FCSTD DOCUMENT  (FreeCAD 1.0R39109 (Git))
Label: Car_roof_Mount
License: All rights reserved
LicenseURL: https://en.wikipedia.org/wiki/All_rights_reserved
objects: Part::Feature×219, Part::Cylinder×108, App::Part×48, Part::MultiFuse×18, Part::Box×15, Part::Cut×6, Part::Torus×5, Part::FeaturePython×4, Part::Fillet×3, TechDraw::DrawSVGTemplate×1, TechDraw::DrawViewPart×1, TechDraw::DrawViewDimension×1, TechDraw::DrawPage×1, Sketcher::SketchObject×1, Part::Extrusion×1
note: 382 computed .brp shape members not serialized (recipe doc carries the construction recipe); baked Part::Feature solids carry a one-line shape summary decoded from their .brp

FEATURE [Part::Box] Box  label="Cube"
  AttacherType = Attacher::AttachEngine3D
  Height = 3.25
  Length = 762
  Placement = pos=(1065,96,7) rot=(0,0,1;1.5708rad)
  Width = 914.4
FEATURE [Part::Cylinder] Cylinder  label="base00"
  Angle = 360
  AttacherType = Attacher::AttachEngine3D
  FirstAngle = 0
  Height = 965.2
  Placement = pos=(12.7,0,0) rot=(-0.57735,0.57735,0.57735;2.0944rad)
  Radius = 12.7
  SecondAngle = 0
FEATURE [Part::Cylinder] Cylinder002  label="base02"
  Angle = 360
  AttacherType = Attacher::AttachEngine3D
  FirstAngle = 0
  Height = 1244.6
  Placement = pos=(0,12.7,0) rot=(0,1,0;1.5708rad)
  Radius = 12.7
  SecondAngle = 0
FEATURE [Part::Cylinder] Cylinder003  label="base03"
  Angle = 360
  AttacherType = Attacher::AttachEngine3D
  FirstAngle = 0
  Height = 1244.6
  Placement = pos=(0,952.5,0) rot=(0,1,0;1.5708rad)
  Radius = 12.7
  SecondAngle = 0
FEATURE [Part::Cylinder] Cylinder004  label="mount01"
  Angle = 360
  AttacherType = Attacher::AttachEngine3D
  FirstAngle = 0
  Height = 76.2
  Placement = pos=(1235.62,12.7,-3.72) rot=(0.382683,0,0.92388;3.14159rad)
  Radius = 12.7
  SecondAngle = 0
FEATURE [Part::Cylinder] Cylinder005  label="mount002"
  Angle = 360
  AttacherType = Attacher::AttachEngine3D
  FirstAngle = 0
  Height = 76.2
  Placement = pos=(1235.62,952.5,-3.72) rot=(0.382683,0,0.92388;3.14159rad)
  Radius = 12.7
  SecondAngle = 0
FEATURE [Part::Torus] Torus
  Angle1 = -180
  Angle2 = 180
  Angle3 = 14.3
  AttacherType = Attacher::AttachEngine3D
  Placement = pos=(-2495,471.5,50.8) rot=(0,0,-1;0.122173rad)
  Radius1 = 3810
  Radius2 = 12.7
FEATURE [Part::Cylinder] Cylinder006  label="base004"
  Angle = 360
  AttacherType = Attacher::AttachEngine3D
  FirstAngle = 0
  Height = 965.2
  Placement = pos=(-63.5,0,76.2) rot=(-0.57735,0.57735,0.57735;2.0944rad)
  Radius = 12.7
  SecondAngle = 0
FEATURE [Part::Torus] Torus001
  Angle1 = -180
  Angle2 = 180
  Angle3 = 16.28
  AttacherType = Attacher::AttachEngine3D
  Placement = pos=(519.042,-57.4562,-4703.18) rot=(0.533716,0.602162,0.593758;4.10898rad)
  Radius1 = 4817.1
  Radius2 = 12.7
FEATURE [Part::Torus] Torus002
  Angle1 = -180
  Angle2 = 180
  Angle3 = 16.28
  AttacherType = Attacher::AttachEngine3D
  Placement = pos=(519.042,889,-4703.18) rot=(0.533716,0.602162,0.593758;4.10898rad)
  Radius1 = 4817.1
  Radius2 = 12.7
FEATURE [Part::Cylinder] Cylinder007  label="base005"
  Angle = 360
  AttacherType = Attacher::AttachEngine3D
  FirstAngle = 0
  Height = 965.2
  Placement = pos=(1089.2,0,0) rot=(0.57735,-0.57735,-0.57735;4.18879rad)
  Radius = 6.35
  SecondAngle = 0
FEATURE [Part::Cylinder] Cylinder008  label="base006"
  Angle = 360
  AttacherType = Attacher::AttachEngine3D
  FirstAngle = 0
  Height = 965.2
  Placement = pos=(919.2,0,0) rot=(0.57735,-0.57735,-0.57735;4.18879rad)
  Radius = 6.35
  SecondAngle = 0
FEATURE [Part::Cylinder] Cylinder009  label="base007"
  Angle = 360
  AttacherType = Attacher::AttachEngine3D
  FirstAngle = 0
  Height = 965.2
  Placement = pos=(749.2,0,0) rot=(0.57735,-0.57735,-0.57735;4.18879rad)
  Radius = 6.35
  SecondAngle = 0
FEATURE [Part::Cylinder] Cylinder010  label="base008"
  Angle = 360
  AttacherType = Attacher::AttachEngine3D
  FirstAngle = 0
  Height = 965.2
  Placement = pos=(579.2,0,0) rot=(0.57735,-0.57735,-0.57735;4.18879rad)
  Radius = 6.35
  SecondAngle = 0
FEATURE [Part::Cylinder] Cylinder011  label="base009"
  Angle = 360
  AttacherType = Attacher::AttachEngine3D
  FirstAngle = 0
  Height = 965.2
  Placement = pos=(409.2,0,0) rot=(0.57735,-0.57735,-0.57735;4.18879rad)
  Radius = 6.35
  SecondAngle = 0
FEATURE [Part::Cylinder] Cylinder012  label="base010"
  Angle = 360
  AttacherType = Attacher::AttachEngine3D
  FirstAngle = 0
  Height = 790
  Placement = pos=(0,149.7,0) rot=(0,1,0;1.5708rad)
  Radius = 6.35
  SecondAngle = 0
FEATURE [Part::Cylinder] Cylinder013  label="base011"
  Angle = 360
  AttacherType = Attacher::AttachEngine3D
  FirstAngle = 0
  Height = 790
  Placement = pos=(0,279.7,0) rot=(0,1,0;1.5708rad)
  Radius = 6.35
  SecondAngle = 0
FEATURE [Part::Cylinder] Cylinder014  label="base012"
  Angle = 360
  AttacherType = Attacher::AttachEngine3D
  FirstAngle = 0
  Height = 790
  Placement = pos=(0,409.7,0) rot=(0,1,0;1.5708rad)
  Radius = 6.35
  SecondAngle = 0
FEATURE [Part::Cylinder] Cylinder015  label="base013"
  Angle = 360
  AttacherType = Attacher::AttachEngine3D
  FirstAngle = 0
  Height = 790
  Placement = pos=(0,539.7,0) rot=(0,1,0;1.5708rad)
  Radius = 6.35
  SecondAngle = 0
FEATURE [Part::Cylinder] Cylinder016  label="base014"
  Angle = 360
  AttacherType = Attacher::AttachEngine3D
  FirstAngle = 0
  Height = 790
  Placement = pos=(0,669.7,0) rot=(0,1,0;1.5708rad)
  Radius = 6.35
  SecondAngle = 0
FEATURE [Part::Cylinder] Cylinder017  label="base015"
  Angle = 360
  AttacherType = Attacher::AttachEngine3D
  FirstAngle = 0
  Height = 790
  Placement = pos=(0,799.7,0) rot=(0,1,0;1.5708rad)
  Radius = 6.35
  SecondAngle = 0
FEATURE [Part::MultiFuse] Fusion001  label="vertical"
  Shapes = -> [Cylinder007,Cylinder008,Cylinder009,Cylinder010,Cylinder011]
FEATURE [Part::Cylinder] Cylinder018  label="base016"
  Angle = 360
  AttacherType = Attacher::AttachEngine3D
  FirstAngle = 0
  Height = 141
  Placement = pos=(784.2,148,0) rot=(0.57735,-0.57735,-0.57735;4.18879rad)
  Radius = 6.35
  SecondAngle = 0
FEATURE [Part::Cylinder] Cylinder019  label="base017"
  Angle = 360
  AttacherType = Attacher::AttachEngine3D
  FirstAngle = 0
  Height = 141
  Placement = pos=(784.2,408,0) rot=(0.57735,-0.57735,-0.57735;4.18879rad)
  Radius = 6.35
  SecondAngle = 0
FEATURE [Part::Cylinder] Cylinder020  label="base018"
  Angle = 360
  AttacherType = Attacher::AttachEngine3D
  FirstAngle = 0
  Height = 141
  Placement = pos=(784.2,668,0) rot=(0.57735,-0.57735,-0.57735;4.18879rad)
  Radius = 6.35
  SecondAngle = 0
FEATURE [Part::MultiFuse] Fusion002  label="horizontal"
  Placement = pos=(0,3,0) rot=(0,0,1;0rad)
  Shapes = -> [Cylinder012,Cylinder013,Cylinder014,Cylinder015,Cylinder016,Cylinder017,Cylinder018,Cylinder019,Cylinder020]
FEATURE [Part::Cylinder] Cylinder021  label="base019"
  Angle = 360
  AttacherType = Attacher::AttachEngine3D
  FirstAngle = 0
  Height = 400
  Placement = pos=(0,149.7,0) rot=(0,1,0;1.5708rad)
  Radius = 6.35
  SecondAngle = 0
FEATURE [Part::Cylinder] Cylinder022  label="base020"
  Angle = 360
  AttacherType = Attacher::AttachEngine3D
  FirstAngle = 0
  Height = 400
  Placement = pos=(0,279.7,0) rot=(0,1,0;1.5708rad)
  Radius = 6.35
  SecondAngle = 0
FEATURE [Part::Cylinder] Cylinder023  label="base021"
  Angle = 360
  AttacherType = Attacher::AttachEngine3D
  FirstAngle = 0
  Height = 400
  Placement = pos=(0,409.7,0) rot=(0,1,0;1.5708rad)
  Radius = 6.35
  SecondAngle = 0
FEATURE [Part::Cylinder] Cylinder024  label="base022"
  Angle = 360
  AttacherType = Attacher::AttachEngine3D
  FirstAngle = 0
  Height = 400
  Placement = pos=(0,539.7,0) rot=(0,1,0;1.5708rad)
  Radius = 6.35
  SecondAngle = 0
FEATURE [Part::Cylinder] Cylinder025  label="base023"
  Angle = 360
  AttacherType = Attacher::AttachEngine3D
  FirstAngle = 0
  Height = 400
  Placement = pos=(0,669.7,0) rot=(0,1,0;1.5708rad)
  Radius = 6.35
  SecondAngle = 0
FEATURE [Part::Cylinder] Cylinder026  label="base024"
  Angle = 360
  AttacherType = Attacher::AttachEngine3D
  FirstAngle = 0
  Height = 400
  Placement = pos=(0,799.7,0) rot=(0,1,0;1.5708rad)
  Radius = 6.35
  SecondAngle = 0
FEATURE [Part::Cylinder] Cylinder027  label="base025"
  Angle = 360
  AttacherType = Attacher::AttachEngine3D
  FirstAngle = 0
  Height = 141
  Placement = pos=(0,665,0) rot=(0.57735,-0.57735,-0.57735;4.18879rad)
  Radius = 6.35
  SecondAngle = 0
FEATURE [Part::Cylinder] Cylinder028  label="base026"
  Angle = 360
  AttacherType = Attacher::AttachEngine3D
  FirstAngle = 0
  Height = 141
  Placement = pos=(0,405,0) rot=(0.57735,-0.57735,-0.57735;4.18879rad)
  Radius = 6.35
  SecondAngle = 0
FEATURE [Part::Cylinder] Cylinder029  label="base027"
  Angle = 360
  AttacherType = Attacher::AttachEngine3D
  FirstAngle = 0
  Height = 141
  Placement = pos=(0,145,0) rot=(0.57735,-0.57735,-0.57735;4.18879rad)
  Radius = 6.35
  SecondAngle = 0
FEATURE [Part::MultiFuse] Fusion003  label="horizontal_front"
  Placement = pos=(824,3,0) rot=(0,0,1;0rad)
  Shapes = -> [Cylinder025,Cylinder026,Cylinder022,Cylinder021,Cylinder023,Cylinder024,Cylinder027,Cylinder029,Cylinder028]
FEATURE [Part::Cylinder] Cylinder030  label="Cylinder"
  Angle = 360
  AttacherType = Attacher::AttachEngine3D
  FirstAngle = 0
  Height = 124.3
  Placement = pos=(409,19,0) rot=(0,-1,0;0.523599rad)
  Radius = 6.35
  SecondAngle = 0
FEATURE [Part::Cylinder] Cylinder031
  Angle = 360
  AttacherType = Attacher::AttachEngine3D
  FirstAngle = 0
  Height = 131.3
  Placement = pos=(579,19,0) rot=(0,-1,0;0.523599rad)
  Radius = 6.35
  SecondAngle = 0
FEATURE [Part::Cylinder] Cylinder032
  Angle = 360
  AttacherType = Attacher::AttachEngine3D
  FirstAngle = 0
  Height = 124.3
  Placement = pos=(749,19,0) rot=(0,-1,0;0.523599rad)
  Radius = 6.35
  SecondAngle = 0
FEATURE [Part::Cylinder] Cylinder033
  Angle = 360
  AttacherType = Attacher::AttachEngine3D
  FirstAngle = 0
  Height = 117.3
  Placement = pos=(919,19,0) rot=(0,-1,0;0.523599rad)
  Radius = 6.35
  SecondAngle = 0
FEATURE [Part::Cylinder] Cylinder034
  Angle = 360
  AttacherType = Attacher::AttachEngine3D
  FirstAngle = 0
  Height = 96.3
  Placement = pos=(1089,19,0) rot=(0,-1,0;0.523599rad)
  Radius = 6.35
  SecondAngle = 0
FEATURE [Part::MultiFuse] Fusion004  label="side_bars_1"
  Shapes = -> [Cylinder030,Cylinder031,Cylinder032,Cylinder033,Cylinder034]
FEATURE [Part::Cylinder] Cylinder035
  Angle = 360
  AttacherType = Attacher::AttachEngine3D
  FirstAngle = 0
  Height = 124.3
  Placement = pos=(409,19,0) rot=(0,-1,0;0.523599rad)
  Radius = 6.35
  SecondAngle = 0
FEATURE [Part::Cylinder] Cylinder036
  Angle = 360
  AttacherType = Attacher::AttachEngine3D
  FirstAngle = 0
  Height = 131.3
  Placement = pos=(579,19,0) rot=(0,-1,0;0.523599rad)
  Radius = 6.35
  SecondAngle = 0
FEATURE [Part::Cylinder] Cylinder037
  Angle = 360
  AttacherType = Attacher::AttachEngine3D
  FirstAngle = 0
  Height = 124.3
  Placement = pos=(749,19,0) rot=(0,-1,0;0.523599rad)
  Radius = 6.35
  SecondAngle = 0
FEATURE [Part::Cylinder] Cylinder038
  Angle = 360
  AttacherType = Attacher::AttachEngine3D
  FirstAngle = 0
  Height = 117.3
  Placement = pos=(919,19,0) rot=(0,-1,0;0.523599rad)
  Radius = 6.35
  SecondAngle = 0
FEATURE [Part::Cylinder] Cylinder039
  Angle = 360
  AttacherType = Attacher::AttachEngine3D
  FirstAngle = 0
  Height = 96.3
  Placement = pos=(1089,19,0) rot=(0,-1,0;0.523599rad)
  Radius = 6.35
  SecondAngle = 0
FEATURE [Part::MultiFuse] Fusion005  label="side_bars_002"
  Placement = pos=(0,936.4,0) rot=(0,0,1;0rad)
  Shapes = -> [Cylinder035,Cylinder036,Cylinder037,Cylinder038,Cylinder039]
FEATURE [Part::Cylinder] Cylinder040 .. Cylinder044  x5 (patterned run collapsed; names and placements below)
  Angle = 360
  AttacherType = Attacher::AttachEngine3D
  FirstAngle = 0
  Height = 124.3
  Radius = 6.35
  SecondAngle = 0
  placements: 5 in arithmetic series — first pos=(17.6777,152.7,-3.53553) rot=(0,-1,0;0.785398rad), step (0,130,0), last pos=(17.6777,672.7,-3.53553) rot=(0,-1,0;0.785398rad)
FEATURE [Part::Cylinder] Cylinder045
  Angle = 360
  AttacherType = Attacher::AttachEngine3D
  FirstAngle = 0
  Height = 100.3
  Placement = pos=(17.6777,152.7,-3.53553) rot=(0,-1,0;0.785398rad)
  Radius = 6.35
  SecondAngle = 0
FEATURE [Part::Cylinder] Cylinder046 .. Cylinder050  x5 (patterned run collapsed; names and placements below)
  Angle = 360
  AttacherType = Attacher::AttachEngine3D
  FirstAngle = 0
  Height = 100
  Radius = 6.35
  SecondAngle = 0
  placements: 5 in arithmetic series — first pos=(17.6777,282.7,-3.53553) rot=(0,-1,0;0.785398rad), step (0,130,0), last pos=(17.6777,802.7,-3.53553) rot=(0,-1,0;0.785398rad)
FEATURE [Part::MultiFuse] Fusion007  label="front_bar"
  Placement = pos=(1229,0,16) rot=(0,1,0;1.8326rad)
  Shapes = -> [Cylinder045,Cylinder046,Cylinder047,Cylinder048,Cylinder049,Cylinder050]
FEATURE [Part::Cylinder] Cylinder051
  Angle = 360
  AttacherType = Attacher::AttachEngine3D
  FirstAngle = 0
  Height = 124.3
  Placement = pos=(17.6777,802.7,-3.53553) rot=(0,-1,0;0.785398rad)
  Radius = 6.35
  SecondAngle = 0
FEATURE [Part::MultiFuse] Fusion006  label="Back_bars"
  Shapes = -> [Cylinder040,Cylinder041,Cylinder042,Cylinder043,Cylinder044,Cylinder051]
FEATURE [Part::Cylinder] Cylinder052  label="base028"
  Angle = 360
  AttacherType = Attacher::AttachEngine3D
  FirstAngle = 0
  Height = 965.2
  Placement = pos=(1080,0,80.5) rot=(-0.57735,0.57735,0.57735;2.0944rad)
  Radius = 12.7
  SecondAngle = 0
FEATURE [Part::MultiFuse] Fusion  label="out_frame"
  Shapes = -> [Cylinder,Cylinder002,Cylinder003,Cylinder005,Cylinder004,Torus,Cylinder006,Torus001,Torus002,Cylinder052]
FEATURE [Part::Feature] Part__Feature042  label="Z_-16147B_ZH-16147B-002"
  shape: bbox 438.9 x 219.4 x 405.1 mm, 3210 faces (baked)
FEATURE [Part::Feature] Part__Feature043  label="INSERTS-016"
  Placement = pos=(-180.975,-168.256,-155.575) rot=(0,0,1;0rad)
  shape: bbox 7.519 x 8.463 x 7.519 mm, 71 faces (baked)
FEATURE [Part::Feature] Part__Feature044  label="INSERTS-017"
  Placement = pos=(-170.872,-174.835,-145.472) rot=(0,0,1;3.14159rad)
  shape: bbox 7.519 x 8.463 x 7.519 mm, 71 faces (baked)
FEATURE [Part::Feature] Part__Feature045  label="INSERTS-018"
  Placement = pos=(-205.994,-3.7592,-180.594) rot=(0,0,1;3.14159rad)
  shape: bbox 7.519 x 8.463 x 7.519 mm, 71 faces (baked)
FEATURE [Part::Feature] Part__Feature046  label="INSERTS-019"
  Placement = pos=(-180.975,-168.083,155.575) rot=(1,0,0;3.14159rad)
  shape: bbox 7.519 x 8.463 x 7.519 mm, 71 faces (baked)
FEATURE [Part::Feature] Part__Feature047  label="INSERTS-020"
  Placement = pos=(-170.872,-175.008,145.472) rot=(0,1,0;3.14159rad)
  shape: bbox 7.519 x 8.463 x 7.519 mm, 71 faces (baked)
FEATURE [Part::Feature] Part__Feature048  label="INSERTS-021"
  Placement = pos=(-205.994,-3.93217,180.594) rot=(0,1,0;3.14159rad)
  shape: bbox 7.519 x 8.463 x 7.519 mm, 71 faces (baked)
FEATURE [Part::Feature] Part__Feature049  label="INSERTS-022"
  Placement = pos=(180.975,-168.083,-155.575) rot=(0,0,1;3.14159rad)
  shape: bbox 7.519 x 8.463 x 7.519 mm, 71 faces (baked)
FEATURE [Part::Feature] Part__Feature050  label="INSERTS-023"
  Placement = pos=(170.872,-175.008,-145.472) rot=(0,0,1;0rad)
  shape: bbox 7.519 x 8.463 x 7.519 mm, 71 faces (baked)
FEATURE [Part::Feature] Part__Feature051  label="INSERTS-024"
  Placement = pos=(205.994,-3.93217,-180.594) rot=(0,0,1;0rad)
  shape: bbox 7.519 x 8.463 x 7.519 mm, 71 faces (baked)
FEATURE [Part::Feature] Part__Feature052  label="INSERTS-025"
  Placement = pos=(180.975,-168.256,155.575) rot=(0,1,0;3.14159rad)
  shape: bbox 7.519 x 8.463 x 7.519 mm, 71 faces (baked)
FEATURE [Part::Feature] Part__Feature053  label="INSERTS-026"
  Placement = pos=(170.872,-174.835,145.472) rot=(1,0,0;3.14159rad)
  shape: bbox 7.519 x 8.463 x 7.519 mm, 71 faces (baked)
FEATURE [Part::Feature] Part__Feature054  label="INSERTS-027"
  Placement = pos=(205.994,-3.7592,180.594) rot=(1,0,0;3.14159rad)
  shape: bbox 7.519 x 8.463 x 7.519 mm, 71 faces (baked)
FEATURE [Part::Feature] Part__Feature055  label="LABEL-105"
  Placement = pos=(-1.221e-12,-20.3197,-180.67) rot=(1,0,0;1.56207rad)
  shape: bbox 63.5 x 38.1 x 0.3833 mm, 10 faces (baked)
FEATURE [Part::Feature] Part__Feature056  label="Z_-16141C_ZH-16141C-002"
  shape: bbox 448.9 x 49.63 x 409 mm, 1738 faces (baked)
FEATURE [Part::Feature] Part__Feature057  label="ZH-1614G001"
  Placement = pos=(0,0.635,6.9e-15) rot=(0,0,1;0rad)
  shape: bbox 434.5 x 6.35 x 383.7 mm, 136 faces (baked)
FEATURE [Part::Feature] Part__Feature058  label="ZH-95P_DEFAULT012"
  Placement = pos=(-205.994,24.2826,-195.302) rot=(-1,0,0;0.785398rad)
  shape: bbox 8.798 x 7.344 x 7.344 mm, 11 faces (baked)
FEATURE [Part::Feature] Part__Feature059  label="ZH-95P_DEFAULT013"
  Placement = pos=(-205.994,24.2826,-195.302) rot=(-1,0,0;0.785398rad)
  shape: bbox 5.931 x 7.648 x 7.648 mm, 141 faces (baked)
FEATURE [Part::Feature] Part__Feature060  label="ZH-01L012"
  shape: bbox 29.67 x 17.48 x 21.58 mm, 91 faces (baked)
FEATURE [Part::Feature] Part__Feature061  label="ZH-01L013"
  Placement = pos=(-3.70922,6.42042,-3.4844) rot=(0,0,1;0rad)
  shape: bbox 38.59 x 15.52 x 29.83 mm, 52 faces (baked)
FEATURE [Part::Feature] Part__Feature062  label="ZH-01L014"
  Placement = pos=(-3.88382,6.40232,-3.4844) rot=(0,0,-1;0.101263rad)
  shape: bbox 5.485 x 8.951 x 26.42 mm, 5 faces (baked)
FEATURE [Part::Feature] Part__Feature063  label="ZH-01L015"
  Placement = pos=(-8.2343,12.9933,-3.4844) rot=(0,0,1;1.04312rad)
  shape: bbox 6.537 x 9.263 x 29.53 mm, 5 faces (baked)
FEATURE [Part::Feature] Part__Feature064  label="ZH-01L016"
  Placement = pos=(-3.70922,6.42042,-3.4844) rot=(0,0,1;0rad)
  shape: bbox 46.02 x 13.5 x 24.63 mm, 66 faces (baked)
FEATURE [Part::Feature] Part__Feature065  label="pan cross head_ai_SCREWS-050"
  Placement = pos=(-170.872,-191.294,-145.472) rot=(-0.002139,-0.002139,0.999995;1.5708rad)
  shape: bbox 10.25 x 22.43 x 10.25 mm, 92 faces (baked)
FEATURE [Part::Feature] Part__Feature066  label="ZH-01L017"
  shape: bbox 29.67 x 17.48 x 21.58 mm, 91 faces (baked)
FEATURE [Part::Feature] Part__Feature067  label="ZH-01L018"
  Placement = pos=(-3.70922,6.42042,-3.4844) rot=(0,0,1;0rad)
  shape: bbox 38.59 x 15.52 x 29.83 mm, 52 faces (baked)
FEATURE [Part::Feature] Part__Feature068  label="ZH-01L019"
  Placement = pos=(-3.88382,6.40232,-3.4844) rot=(0,0,-1;0.101263rad)
  shape: bbox 5.485 x 8.951 x 26.42 mm, 5 faces (baked)
FEATURE [Part::Feature] Part__Feature069  label="ZH-01L020"
  Placement = pos=(-8.2343,12.9933,-3.4844) rot=(0,0,1;1.04312rad)
  shape: bbox 6.537 x 9.263 x 29.53 mm, 5 faces (baked)
FEATURE [Part::Feature] Part__Feature070  label="ZH-01L021"
  Placement = pos=(-3.70922,6.42042,-3.4844) rot=(0,0,1;0rad)
  shape: bbox 46.02 x 13.5 x 24.63 mm, 66 faces (baked)
FEATURE [Part::Feature] Part__Feature071  label="pan cross head_ai_SCREWS-051"
  Placement = pos=(-170.872,-191.294,145.472) rot=(0.002139,0.002139,0.999995;1.5708rad)
  shape: bbox 10.25 x 22.43 x 10.25 mm, 92 faces (baked)
FEATURE [Part::Feature] Part__Feature072  label="pan cross head_ai_SCREWS-052"
  Placement = pos=(170.872,-191.294,-145.472) rot=(0.707106,0.707106,-0.001512;3.14462rad)
  shape: bbox 10.25 x 22.43 x 10.25 mm, 92 faces (baked)
FEATURE [Part::Feature] Part__Feature073  label="pan cross head_ai_SCREWS-053"
  Placement = pos=(170.872,-191.294,145.472) rot=(0.707106,0.707106,0.001512;3.13857rad)
  shape: bbox 10.25 x 22.43 x 10.25 mm, 92 faces (baked)
FEATURE [Part::Feature] Part__Feature074  label="ZH-95P_DEFAULT014"
  Placement = pos=(205.994,24.2826,-195.302) rot=(-1,0,0;0.785398rad)
  shape: bbox 8.798 x 7.344 x 7.344 mm, 11 faces (baked)
FEATURE [Part::Feature] Part__Feature075  label="ZH-95P_DEFAULT015"
  Placement = pos=(205.994,24.2826,-195.302) rot=(-1,0,0;0.785398rad)
  shape: bbox 5.931 x 7.648 x 7.648 mm, 141 faces (baked)
FEATURE [Part::Feature] Part__Feature076  label="ZH-95P_DEFAULT016"
  Placement = pos=(-205.994,279.681,60.096) rot=(-1,0,0;0.785398rad)
  shape: bbox 8.798 x 7.344 x 7.344 mm, 11 faces (baked)
FEATURE [Part::Feature] Part__Feature077  label="ZH-95P_DEFAULT017"
  Placement = pos=(-205.994,279.681,60.096) rot=(-1,0,0;0.785398rad)
  shape: bbox 5.931 x 7.648 x 7.648 mm, 141 faces (baked)
FEATURE [Part::Feature] Part__Feature078  label="ZH-95P_DEFAULT018"
  Placement = pos=(205.994,279.681,60.096) rot=(-1,0,0;0.785398rad)
  shape: bbox 8.798 x 7.344 x 7.344 mm, 11 faces (baked)
FEATURE [Part::Feature] Part__Feature079  label="ZH-95P_DEFAULT019"
  Placement = pos=(205.994,279.681,60.096) rot=(-1,0,0;0.785398rad)
  shape: bbox 5.931 x 7.648 x 7.648 mm, 141 faces (baked)
FEATURE [App::Part] ZH_01L002  label="ZH-01L022"
  Group = -> [Part__Feature060,Part__Feature061,Part__Feature062,Part__Feature063,Part__Feature064]
  Origin = -> Origin013
  Placement = pos=(-130.048,-7.112,192.024) rot=(0.579853,0.572312,0.579853;2.10197rad)
FEATURE [App::Part] ZH_01L003  label="ZH-01L023"
  Group = -> [Part__Feature066,Part__Feature067,Part__Feature068,Part__Feature069,Part__Feature070]
  Origin = -> Origin014
  Placement = pos=(130.048,-7.112,192.024) rot=(0.579853,0.572312,0.579853;2.10197rad)
FEATURE [App::Part] ZH_95P_DEFAULT004  label="ZH-95P_DEFAULT020"
  Group = -> [Part__Feature058,Part__Feature059]
  Origin = -> Origin012
FEATURE [App::Part] ZH_95P_DEFAULT005  label="ZH-95P_DEFAULT021"
  Group = -> [Part__Feature074,Part__Feature075]
  Origin = -> Origin015
FEATURE [App::Part] ZH_95P_DEFAULT006  label="ZH-95P_DEFAULT022"
  Group = -> [Part__Feature076,Part__Feature077]
  Origin = -> Origin016
FEATURE [App::Part] ZH_95P_DEFAULT007  label="ZH-95P_DEFAULT023"
  Group = -> [Part__Feature078,Part__Feature079]
  Origin = -> Origin017
FEATURE [App::Part] Z__16147BI_ZH_16147BI_002  label="Z_-16147BI_ZH-16147BI-002"
  Group = -> [Part__Feature042,Part__Feature043,Part__Feature044,Part__Feature045,Part__Feature046,Part__Feature047,Part__Feature048,Part__Feature049,Part__Feature050,Part__Feature051,Part__Feature052,Part__Feature053,Part__Feature054,Part__Feature055]
  Origin = -> Origin010
FEATURE [Part::Feature] Part__Feature080  label="Z_-16147B_ZH-16147B-003"
  shape: bbox 438.9 x 219.4 x 405.1 mm, 3210 faces (baked)
FEATURE [Part::Feature] Part__Feature081  label="INSERTS-028"
  Placement = pos=(-180.975,-168.256,-155.575) rot=(0,0,1;0rad)
  shape: bbox 7.519 x 8.463 x 7.519 mm, 71 faces (baked)
FEATURE [Part::Feature] Part__Feature082  label="INSERTS-029"
  Placement = pos=(-170.872,-174.835,-145.472) rot=(0,0,1;3.14159rad)
  shape: bbox 7.519 x 8.463 x 7.519 mm, 71 faces (baked)
FEATURE [Part::Feature] Part__Feature083  label="INSERTS-030"
  Placement = pos=(-205.994,-3.7592,-180.594) rot=(0,0,1;3.14159rad)
  shape: bbox 7.519 x 8.463 x 7.519 mm, 71 faces (baked)
FEATURE [Part::Feature] Part__Feature084  label="INSERTS-031"
  Placement = pos=(-180.975,-168.083,155.575) rot=(1,0,0;3.14159rad)
  shape: bbox 7.519 x 8.463 x 7.519 mm, 71 faces (baked)
FEATURE [Part::Feature] Part__Feature085  label="INSERTS-032"
  Placement = pos=(-170.872,-175.008,145.472) rot=(0,1,0;3.14159rad)
  shape: bbox 7.519 x 8.463 x 7.519 mm, 71 faces (baked)
FEATURE [Part::Feature] Part__Feature086  label="INSERTS-033"
  Placement = pos=(-205.994,-3.93217,180.594) rot=(0,1,0;3.14159rad)
  shape: bbox 7.519 x 8.463 x 7.519 mm, 71 faces (baked)
FEATURE [Part::Feature] Part__Feature087  label="INSERTS-034"
  Placement = pos=(180.975,-168.083,-155.575) rot=(0,0,1;3.14159rad)
  shape: bbox 7.519 x 8.463 x 7.519 mm, 71 faces (baked)
FEATURE [Part::Feature] Part__Feature088  label="INSERTS-035"
  Placement = pos=(170.872,-175.008,-145.472) rot=(0,0,1;0rad)
  shape: bbox 7.519 x 8.463 x 7.519 mm, 71 faces (baked)
FEATURE [Part::Feature] Part__Feature089  label="INSERTS-036"
  Placement = pos=(205.994,-3.93217,-180.594) rot=(0,0,1;0rad)
  shape: bbox 7.519 x 8.463 x 7.519 mm, 71 faces (baked)
FEATURE [Part::Feature] Part__Feature090  label="INSERTS-037"
  Placement = pos=(180.975,-168.256,155.575) rot=(0,1,0;3.14159rad)
  shape: bbox 7.519 x 8.463 x 7.519 mm, 71 faces (baked)
FEATURE [Part::Feature] Part__Feature091  label="INSERTS-038"
  Placement = pos=(170.872,-174.835,145.472) rot=(1,0,0;3.14159rad)
  shape: bbox 7.519 x 8.463 x 7.519 mm, 71 faces (baked)
FEATURE [Part::Feature] Part__Feature092  label="INSERTS-039"
  Placement = pos=(205.994,-3.7592,180.594) rot=(1,0,0;3.14159rad)
  shape: bbox 7.519 x 8.463 x 7.519 mm, 71 faces (baked)
FEATURE [Part::Feature] Part__Feature093  label="LABEL-106"
  Placement = pos=(-1.221e-12,-20.3197,-180.67) rot=(1,0,0;1.56207rad)
  shape: bbox 63.5 x 38.1 x 0.3833 mm, 10 faces (baked)
FEATURE [Part::Feature] Part__Feature094  label="Z_-16141C_ZH-16141C-003"
  shape: bbox 448.9 x 49.63 x 409 mm, 1738 faces (baked)
FEATURE [Part::Feature] Part__Feature095  label="ZH-1614G002"
  Placement = pos=(0,0.635,6.9e-15) rot=(0,0,1;0rad)
  shape: bbox 434.5 x 6.35 x 383.7 mm, 136 faces (baked)
FEATURE [Part::Feature] Part__Feature096  label="ZH-95P_DEFAULT024"
  Placement = pos=(-205.994,24.2826,-195.302) rot=(-1,0,0;0.785398rad)
  shape: bbox 8.798 x 7.344 x 7.344 mm, 11 faces (baked)
FEATURE [Part::Feature] Part__Feature097  label="ZH-95P_DEFAULT025"
  Placement = pos=(-205.994,24.2826,-195.302) rot=(-1,0,0;0.785398rad)
  shape: bbox 5.931 x 7.648 x 7.648 mm, 141 faces (baked)
FEATURE [Part::Feature] Part__Feature098  label="ZH-01L024"
  shape: bbox 29.67 x 17.48 x 21.58 mm, 91 faces (baked)
FEATURE [Part::Feature] Part__Feature099  label="ZH-01L025"
  Placement = pos=(-3.70922,6.42042,-3.4844) rot=(0,0,1;0rad)
  shape: bbox 38.59 x 15.52 x 29.83 mm, 52 faces (baked)
FEATURE [Part::Feature] Part__Feature100  label="ZH-01L026"
  Placement = pos=(-3.88382,6.40232,-3.4844) rot=(0,0,-1;0.101263rad)
  shape: bbox 5.485 x 8.951 x 26.42 mm, 5 faces (baked)
FEATURE [Part::Feature] Part__Feature101  label="ZH-01L027"
  Placement = pos=(-8.2343,12.9933,-3.4844) rot=(0,0,1;1.04312rad)
  shape: bbox 6.537 x 9.263 x 29.53 mm, 5 faces (baked)
FEATURE [Part::Feature] Part__Feature102  label="ZH-01L028"
  Placement = pos=(-3.70922,6.42042,-3.4844) rot=(0,0,1;0rad)
  shape: bbox 46.02 x 13.5 x 24.63 mm, 66 faces (baked)
FEATURE [Part::Feature] Part__Feature103  label="pan cross head_ai_SCREWS-054"
  Placement = pos=(-170.872,-191.294,-145.472) rot=(-0.002139,-0.002139,0.999995;1.5708rad)
  shape: bbox 10.25 x 22.43 x 10.25 mm, 92 faces (baked)
FEATURE [Part::Feature] Part__Feature104  label="ZH-01L029"
  shape: bbox 29.67 x 17.48 x 21.58 mm, 91 faces (baked)
FEATURE [Part::Feature] Part__Feature105  label="ZH-01L030"
  Placement = pos=(-3.70922,6.42042,-3.4844) rot=(0,0,1;0rad)
  shape: bbox 38.59 x 15.52 x 29.83 mm, 52 faces (baked)
FEATURE [Part::Feature] Part__Feature106  label="ZH-01L031"
  Placement = pos=(-3.88382,6.40232,-3.4844) rot=(0,0,-1;0.101263rad)
  shape: bbox 5.485 x 8.951 x 26.42 mm, 5 faces (baked)
FEATURE [Part::Feature] Part__Feature107  label="ZH-01L032"
  Placement = pos=(-8.2343,12.9933,-3.4844) rot=(0,0,1;1.04312rad)
  shape: bbox 6.537 x 9.263 x 29.53 mm, 5 faces (baked)
FEATURE [Part::Feature] Part__Feature108  label="ZH-01L033"
  Placement = pos=(-3.70922,6.42042,-3.4844) rot=(0,0,1;0rad)
  shape: bbox 46.02 x 13.5 x 24.63 mm, 66 faces (baked)
FEATURE [Part::Feature] Part__Feature109  label="pan cross head_ai_SCREWS-055"
  Placement = pos=(-170.872,-191.294,145.472) rot=(0.002139,0.002139,0.999995;1.5708rad)
  shape: bbox 10.25 x 22.43 x 10.25 mm, 92 faces (baked)
FEATURE [Part::Feature] Part__Feature110  label="pan cross head_ai_SCREWS-056"
  Placement = pos=(170.872,-191.294,-145.472) rot=(0.707106,0.707106,-0.001512;3.14462rad)
  shape: bbox 10.25 x 22.43 x 10.25 mm, 92 faces (baked)
FEATURE [Part::Feature] Part__Feature111  label="pan cross head_ai_SCREWS-057"
  Placement = pos=(170.872,-191.294,145.472) rot=(0.707106,0.707106,0.001512;3.13857rad)
  shape: bbox 10.25 x 22.43 x 10.25 mm, 92 faces (baked)
FEATURE [Part::Feature] Part__Feature112  label="ZH-95P_DEFAULT026"
  Placement = pos=(205.994,24.2826,-195.302) rot=(-1,0,0;0.785398rad)
  shape: bbox 8.798 x 7.344 x 7.344 mm, 11 faces (baked)
FEATURE [Part::Feature] Part__Feature113  label="ZH-95P_DEFAULT027"
  Placement = pos=(205.994,24.2826,-195.302) rot=(-1,0,0;0.785398rad)
  shape: bbox 5.931 x 7.648 x 7.648 mm, 141 faces (baked)
FEATURE [Part::Feature] Part__Feature114  label="ZH-95P_DEFAULT028"
  Placement = pos=(-205.994,279.681,60.096) rot=(-1,0,0;0.785398rad)
  shape: bbox 8.798 x 7.344 x 7.344 mm, 11 faces (baked)
FEATURE [Part::Feature] Part__Feature115  label="ZH-95P_DEFAULT029"
  Placement = pos=(-205.994,279.681,60.096) rot=(-1,0,0;0.785398rad)
  shape: bbox 5.931 x 7.648 x 7.648 mm, 141 faces (baked)
FEATURE [Part::Feature] Part__Feature116  label="ZH-95P_DEFAULT030"
  Placement = pos=(205.994,279.681,60.096) rot=(-1,0,0;0.785398rad)
  shape: bbox 8.798 x 7.344 x 7.344 mm, 11 faces (baked)
FEATURE [Part::Feature] Part__Feature117  label="ZH-95P_DEFAULT031"
  Placement = pos=(205.994,279.681,60.096) rot=(-1,0,0;0.785398rad)
  shape: bbox 5.931 x 7.648 x 7.648 mm, 141 faces (baked)
FEATURE [App::Part] ZH_01L004  label="ZH-01L034"
  Group = -> [Part__Feature098,Part__Feature099,Part__Feature100,Part__Feature101,Part__Feature102]
  Origin = -> Origin022
  Placement = pos=(-130.048,-7.112,192.024) rot=(0.579853,0.572312,0.579853;2.10197rad)
FEATURE [App::Part] ZH_01L005  label="ZH-01L035"
  Group = -> [Part__Feature104,Part__Feature105,Part__Feature106,Part__Feature107,Part__Feature108]
  Origin = -> Origin023
  Placement = pos=(130.048,-7.112,192.024) rot=(0.579853,0.572312,0.579853;2.10197rad)
FEATURE [App::Part] ZH_95P_DEFAULT008  label="ZH-95P_DEFAULT032"
  Group = -> [Part__Feature096,Part__Feature097]
  Origin = -> Origin021
FEATURE [App::Part] ZH_95P_DEFAULT009  label="ZH-95P_DEFAULT033"
  Group = -> [Part__Feature112,Part__Feature113]
  Origin = -> Origin024
FEATURE [App::Part] ZH_95P_DEFAULT010  label="ZH-95P_DEFAULT034"
  Group = -> [Part__Feature114,Part__Feature115]
  Origin = -> Origin025
FEATURE [App::Part] ZH_95P_DEFAULT011  label="ZH-95P_DEFAULT035"
  Group = -> [Part__Feature116,Part__Feature117]
  Origin = -> Origin026
FEATURE [App::Part] Z__16141CG_ZH_16141CG_003  label="Z_-16141CG_ZH-16141CG-003"
  Group = -> [Part__Feature094,Part__Feature095]
  Origin = -> Origin020
  Placement = pos=(0,144.582,-60.2035) rot=(-1,0,0;0.785398rad)
FEATURE [App::Part] Z__16147BI_ZH_16147BI_003  label="Z_-16147BI_ZH-16147BI-003"
  Group = -> [Part__Feature080,Part__Feature081,Part__Feature082,Part__Feature083,Part__Feature084,Part__Feature085,Part__Feature086,Part__Feature087,Part__Feature088,Part__Feature089,Part__Feature090,Part__Feature091,Part__Feature092,Part__Feature093]
  Origin = -> Origin019
FEATURE [App::Part] ZH_161407_003  label="Frnt_Rht_ZH-161407"
  Group = -> [Z__16147BI_ZH_16147BI_003,Z__16141CG_ZH_16141CG_003,ZH_95P_DEFAULT008,ZH_01L004,Part__Feature103,ZH_01L005,Part__Feature109,Part__Feature110,Part__Feature111,ZH_95P_DEFAULT009,ZH_95P_DEFAULT010,ZH_95P_DEFAULT011]
  Origin = -> Origin027
  Placement = pos=(815,265,195) rot=(1,0,0;1.5708rad)
FEATURE [App::Part] Z__16141CG_ZH_16141CG_002  label="Z_-16141CG_ZH-16141CG-002"
  Group = -> [Part__Feature056,Part__Feature057]
  Origin = -> Origin011
  Placement = pos=(0,144.582,-60.2035) rot=(-1,0,0;0.785398rad)
FEATURE [App::Part] ZH_161407_002  label="Frnt_Lft_ZH-161407"
  Group = -> [Z__16147BI_ZH_16147BI_002,Z__16141CG_ZH_16141CG_002,ZH_95P_DEFAULT004,ZH_01L002,Part__Feature065,ZH_01L003,Part__Feature071,Part__Feature072,Part__Feature073,ZH_95P_DEFAULT005,ZH_95P_DEFAULT006,ZH_95P_DEFAULT007]
  Origin = -> Origin018
  Placement = pos=(815,685,195) rot=(0,0.707107,0.707107;3.14159rad)
FEATURE [Part::Feature] Part__Feature  label="Z_-14126B_ZH-14126B-01"
  shape: bbox 388.1 x 188 x 354.3 mm, 3639 faces (baked)
FEATURE [Part::Feature] Part__Feature001  label="INSERTS-4"
  Placement = pos=(-155.575,-142.062,-130.175) rot=(0,0,1;0rad)
  shape: bbox 7.519 x 8.64 x 7.519 mm, 80 faces (baked)
FEATURE [Part::Feature] Part__Feature002  label="INSERTS-005"
  Placement = pos=(-146.05,-148.641,-120.65) rot=(0,0,1;3.14159rad)
  shape: bbox 7.519 x 8.64 x 7.519 mm, 80 faces (baked)
FEATURE [Part::Feature] Part__Feature003  label="INSERTS-006"
  Placement = pos=(-180.594,-3.7592,-155.194) rot=(0,0,1;3.14159rad)
  shape: bbox 7.519 x 8.64 x 7.519 mm, 80 faces (baked)
FEATURE [Part::Feature] Part__Feature004  label="INSERTS-007"
  Placement = pos=(-155.575,-142.062,130.213) rot=(0,0,1;0rad)
  shape: bbox 7.519 x 8.64 x 7.519 mm, 80 faces (baked)
FEATURE [Part::Feature] Part__Feature005  label="INSERTS-008"
  Placement = pos=(-146.05,-148.641,120.688) rot=(0,0,1;3.14159rad)
  shape: bbox 7.519 x 8.64 x 7.519 mm, 80 faces (baked)
FEATURE [Part::Feature] Part__Feature006  label="INSERTS-009"
  Placement = pos=(-180.594,-3.7592,155.232) rot=(0,0,1;3.14159rad)
  shape: bbox 7.519 x 8.64 x 7.519 mm, 80 faces (baked)
FEATURE [Part::Feature] Part__Feature007  label="INSERTS-010"
  Placement = pos=(155.575,-142.062,-130.213) rot=(0,1,0;3.14159rad)
  shape: bbox 7.519 x 8.64 x 7.519 mm, 80 faces (baked)
FEATURE [Part::Feature] Part__Feature008  label="INSERTS-011"
  Placement = pos=(146.05,-148.641,-120.688) rot=(1,0,0;3.14159rad)
  shape: bbox 7.519 x 8.64 x 7.519 mm, 80 faces (baked)
FEATURE [Part::Feature] Part__Feature009  label="INSERTS-012"
  Placement = pos=(180.594,-3.7592,-155.232) rot=(1,0,0;3.14159rad)
  shape: bbox 7.519 x 8.64 x 7.519 mm, 80 faces (baked)
FEATURE [Part::Feature] Part__Feature010  label="INSERTS-013"
  Placement = pos=(155.575,-142.062,130.175) rot=(0,1,0;3.14159rad)
  shape: bbox 7.519 x 8.64 x 7.519 mm, 80 faces (baked)
FEATURE [Part::Feature] Part__Feature011  label="INSERTS-014"
  Placement = pos=(146.05,-148.641,120.65) rot=(1,0,0;3.14159rad)
  shape: bbox 7.519 x 8.64 x 7.519 mm, 80 faces (baked)
FEATURE [Part::Feature] Part__Feature012  label="INSERTS-015"
  Placement = pos=(180.594,-3.7592,155.194) rot=(1,0,0;3.14159rad)
  shape: bbox 7.519 x 8.64 x 7.519 mm, 80 faces (baked)
FEATURE [Part::Feature] Part__Feature013  label="LABEL-104"
  Placement = pos=(-1e-15,-27.9395,-155.204) rot=(1,0,0;1.56207rad)
  shape: bbox 69.85 x 50.8 x 0.4941 mm, 10 faces (baked)
FEATURE [Part::Feature] Part__Feature014  label="Z_-14121C_ZH-14121C-02"
  shape: bbox 398.3 x 44.08 x 358.3 mm, 1962 faces (baked)
FEATURE [Part::Feature] Part__Feature015  label="ZH-1412G"
  Placement = pos=(0,0.635,0) rot=(0,0,1;0rad)
  shape: bbox 383.7 x 6.35 x 332.9 mm, 136 faces (baked)
FEATURE [Part::Feature] Part__Feature016  label="ZH-95P_DEFAULT"
  Placement = pos=(-180.594,11.2268,-155.194) rot=(0,0,1;0rad)
  shape: bbox 8.798 x 6.858 x 8.798 mm, 18 faces (baked)
FEATURE [Part::Feature] Part__Feature017  label="ZH-95P_DEFAULT001"
  Placement = pos=(-180.594,11.2268,-155.194) rot=(0,0,1;0rad)
  shape: bbox 5.931 x 5.698 x 5.931 mm, 154 faces (baked)
FEATURE [Part::Feature] Part__Feature018  label="ZH-01L1"
  shape: bbox 29.67 x 17.48 x 21.58 mm, 95 faces (baked)
FEATURE [Part::Feature] Part__Feature019  label="ZH-01L2"
  Placement = pos=(-3.70922,6.42042,-3.4844) rot=(0,0,1;0rad)
  shape: bbox 38.59 x 15.52 x 29.83 mm, 54 faces (baked)
FEATURE [Part::Feature] Part__Feature020  label="ZH-01L3"
  Placement = pos=(-3.88382,6.40232,-3.4844) rot=(0,0,-1;0.101263rad)
  shape: bbox 5.485 x 8.951 x 26.42 mm, 8 faces (baked)
FEATURE [Part::Feature] Part__Feature021  label="ZH-01L4"
  Placement = pos=(-8.2343,12.9933,-3.4844) rot=(0,0,1;1.04312rad)
  shape: bbox 6.537 x 9.263 x 29.53 mm, 8 faces (baked)
FEATURE [Part::Feature] Part__Feature022  label="ZH-01L5"
  Placement = pos=(-3.70922,6.42042,-3.4844) rot=(0,0,1;0rad)
  shape: bbox 46.02 x 13.5 x 24.63 mm, 70 faces (baked)
FEATURE [Part::Feature] Part__Feature023  label="ZH-01L006"
  shape: bbox 29.67 x 17.48 x 21.58 mm, 95 faces (baked)
FEATURE [Part::Feature] Part__Feature024  label="ZH-01L007"
  Placement = pos=(-3.70922,6.42042,-3.4844) rot=(0,0,1;0rad)
  shape: bbox 38.59 x 15.52 x 29.83 mm, 54 faces (baked)
FEATURE [Part::Feature] Part__Feature025  label="ZH-01L008"
  Placement = pos=(-3.88382,6.40232,-3.4844) rot=(0,0,-1;0.101263rad)
  shape: bbox 5.485 x 8.951 x 26.42 mm, 8 faces (baked)
FEATURE [Part::Feature] Part__Feature026  label="ZH-01L009"
  Placement = pos=(-8.2343,12.9933,-3.4844) rot=(0,0,1;1.04312rad)
  shape: bbox 6.537 x 9.263 x 29.53 mm, 8 faces (baked)
FEATURE [Part::Feature] Part__Feature027  label="ZH-01L010"
  Placement = pos=(-3.70922,6.42042,-3.4844) rot=(0,0,1;0rad)
  shape: bbox 46.02 x 13.5 x 24.63 mm, 70 faces (baked)
FEATURE [Part::Feature] Part__Feature028  label="ZH-95P_DEFAULT003"
  Placement = pos=(180.594,11.2268,-155.194) rot=(0,0,1;0rad)
  shape: bbox 8.798 x 6.858 x 8.798 mm, 18 faces (baked)
FEATURE [Part::Feature] Part__Feature029  label="ZH-95P_DEFAULT004"
  Placement = pos=(180.594,11.2268,-155.194) rot=(0,0,1;0rad)
  shape: bbox 5.931 x 5.698 x 5.931 mm, 154 faces (baked)
FEATURE [Part::Feature] Part__Feature030  label="ZH-95P_DEFAULT006"
  Placement = pos=(-180.594,11.2268,155.194) rot=(0,0,1;0rad)
  shape: bbox 8.798 x 6.858 x 8.798 mm, 18 faces (baked)
FEATURE [Part::Feature] Part__Feature031  label="ZH-95P_DEFAULT007"
  Placement = pos=(-180.594,11.2268,155.194) rot=(0,0,1;0rad)
  shape: bbox 5.931 x 5.698 x 5.931 mm, 154 faces (baked)
FEATURE [Part::Feature] Part__Feature032  label="ZH-95P_DEFAULT009"
  Placement = pos=(180.594,11.2268,155.194) rot=(0,0,1;0rad)
  shape: bbox 8.798 x 6.858 x 8.798 mm, 18 faces (baked)
FEATURE [Part::Feature] Part__Feature033  label="ZH-95P_DEFAULT010"
  Placement = pos=(180.594,11.2268,155.194) rot=(0,0,1;0rad)
  shape: bbox 5.931 x 5.698 x 5.931 mm, 154 faces (baked)
FEATURE [Part::Feature] Part__Feature034  label="SCREWS-049_SCREWS-049"
  Placement = pos=(-146.05,-157.759,-120.65) rot=(0.57735,0.57735,0.57735;2.0944rad)
  shape: bbox 10.25 x 12.9 x 10.25 mm, 23 faces (baked)
FEATURE [Part::Feature] Part__Feature035  label="SCREWS-049_SCREWS-050"
  Placement = pos=(146.05,-157.759,-120.65) rot=(0.57735,0.57735,0.57735;2.0944rad)
  shape: bbox 10.25 x 12.9 x 10.25 mm, 23 faces (baked)
FEATURE [Part::Feature] Part__Feature036  label="SCREWS-049_SCREWS-051"
  Placement = pos=(-146.05,-157.759,120.65) rot=(0.57735,0.57735,-0.57735;4.18879rad)
  shape: bbox 10.25 x 12.9 x 10.25 mm, 23 faces (baked)
FEATURE [Part::Feature] Part__Feature037  label="SCREWS-049_SCREWS-052"
  Placement = pos=(146.05,-157.759,120.65) rot=(-0.57735,-0.57735,0.57735;2.0944rad)
  shape: bbox 10.25 x 12.9 x 10.25 mm, 23 faces (baked)
FEATURE [App::Part] ZH_01L  label="ZH-01L"
  Group = -> [Part__Feature018,Part__Feature019,Part__Feature020,Part__Feature021,Part__Feature022]
  Origin = -> Origin003
  Placement = pos=(-104.648,-7.112,166.624) rot=(0.579853,0.572312,0.579853;2.10197rad)
FEATURE [App::Part] ZH_01L001  label="ZH-01L011"
  Group = -> [Part__Feature023,Part__Feature024,Part__Feature025,Part__Feature026,Part__Feature027]
  Origin = -> Origin004
  Placement = pos=(104.648,-7.112,166.624) rot=(0.579853,0.572312,0.579853;2.10197rad)
FEATURE [App::Part] ZH_95P_DEFAULT  label="ZH-95P_DEFAULT002"
  Group = -> [Part__Feature016,Part__Feature017]
  Origin = -> Origin002
FEATURE [App::Part] ZH_95P_DEFAULT001  label="ZH-95P_DEFAULT005"
  Group = -> [Part__Feature028,Part__Feature029]
  Origin = -> Origin005
FEATURE [App::Part] ZH_95P_DEFAULT002  label="ZH-95P_DEFAULT008"
  Group = -> [Part__Feature030,Part__Feature031]
  Origin = -> Origin006
FEATURE [App::Part] ZH_95P_DEFAULT003  label="ZH-95P_DEFAULT011"
  Group = -> [Part__Feature032,Part__Feature033]
  Origin = -> Origin007
FEATURE [App::Part] Z__14121CG_ZH_14121CG_02  label="Z_-14121CG_ZH-14121CG-02"
  Group = -> [Part__Feature014,Part__Feature015]
  Origin = -> Origin001
  Placement = pos=(0,0.762,0) rot=(0,0,1;0rad)
FEATURE [App::Part] Z__14126BI_ZH_14126BI_01  label="Z_-14126BI_ZH-14126BI-01"
  Group = -> [Part__Feature,Part__Feature001,Part__Feature002,Part__Feature003,Part__Feature004,Part__Feature005,Part__Feature006,Part__Feature007,Part__Feature008,Part__Feature009,Part__Feature010,Part__Feature011,Part__Feature012,Part__Feature013]
  Origin = -> Origin028
FEATURE [App::Part] ZH_141206_92  label="ZH-141206-92"
  Group = -> [Z__14126BI_ZH_14126BI_01,Z__14121CG_ZH_14121CG_02,ZH_95P_DEFAULT,ZH_01L,ZH_01L001,ZH_95P_DEFAULT001,ZH_95P_DEFAULT002,ZH_95P_DEFAULT003,Part__Feature034,Part__Feature035,Part__Feature036,Part__Feature037]
  Origin = -> Origin008
  Placement = pos=(370,290,163) rot=(1,0,0;1.5708rad)
FEATURE [Part::Feature] Part__Feature118  label="Z_-14126B_ZH-14126B-002"
  shape: bbox 388.1 x 188 x 354.3 mm, 3639 faces (baked)
FEATURE [Part::Feature] Part__Feature119  label="INSERTS-040"
  Placement = pos=(-155.575,-142.062,-130.175) rot=(0,0,1;0rad)
  shape: bbox 7.519 x 8.64 x 7.519 mm, 80 faces (baked)
FEATURE [Part::Feature] Part__Feature120  label="INSERTS-041"
  Placement = pos=(-146.05,-148.641,-120.65) rot=(0,0,1;3.14159rad)
  shape: bbox 7.519 x 8.64 x 7.519 mm, 80 faces (baked)
FEATURE [Part::Feature] Part__Feature121  label="INSERTS-042"
  Placement = pos=(-180.594,-3.7592,-155.194) rot=(0,0,1;3.14159rad)
  shape: bbox 7.519 x 8.64 x 7.519 mm, 80 faces (baked)
FEATURE [Part::Feature] Part__Feature122  label="INSERTS-043"
  Placement = pos=(-155.575,-142.062,130.213) rot=(0,0,1;0rad)
  shape: bbox 7.519 x 8.64 x 7.519 mm, 80 faces (baked)
FEATURE [Part::Feature] Part__Feature123  label="INSERTS-044"
  Placement = pos=(-146.05,-148.641,120.688) rot=(0,0,1;3.14159rad)
  shape: bbox 7.519 x 8.64 x 7.519 mm, 80 faces (baked)
FEATURE [Part::Feature] Part__Feature124  label="INSERTS-045"
  Placement = pos=(-180.594,-3.7592,155.232) rot=(0,0,1;3.14159rad)
  shape: bbox 7.519 x 8.64 x 7.519 mm, 80 faces (baked)
FEATURE [Part::Feature] Part__Feature125  label="INSERTS-046"
  Placement = pos=(155.575,-142.062,-130.213) rot=(0,1,0;3.14159rad)
  shape: bbox 7.519 x 8.64 x 7.519 mm, 80 faces (baked)
FEATURE [Part::Feature] Part__Feature126  label="INSERTS-047"
  Placement = pos=(146.05,-148.641,-120.688) rot=(1,0,0;3.14159rad)
  shape: bbox 7.519 x 8.64 x 7.519 mm, 80 faces (baked)
FEATURE [Part::Feature] Part__Feature127  label="INSERTS-048"
  Placement = pos=(180.594,-3.7592,-155.232) rot=(1,0,0;3.14159rad)
  shape: bbox 7.519 x 8.64 x 7.519 mm, 80 faces (baked)
FEATURE [Part::Feature] Part__Feature128  label="INSERTS-049"
  Placement = pos=(155.575,-142.062,130.175) rot=(0,1,0;3.14159rad)
  shape: bbox 7.519 x 8.64 x 7.519 mm, 80 faces (baked)
FEATURE [Part::Feature] Part__Feature129  label="INSERTS-050"
  Placement = pos=(146.05,-148.641,120.65) rot=(1,0,0;3.14159rad)
  shape: bbox 7.519 x 8.64 x 7.519 mm, 80 faces (baked)
FEATURE [Part::Feature] Part__Feature130  label="INSERTS-051"
  Placement = pos=(180.594,-3.7592,155.194) rot=(1,0,0;3.14159rad)
  shape: bbox 7.519 x 8.64 x 7.519 mm, 80 faces (baked)
FEATURE [Part::Feature] Part__Feature131  label="LABEL-107"
  Placement = pos=(-1e-15,-27.9395,-155.204) rot=(1,0,0;1.56207rad)
  shape: bbox 69.85 x 50.8 x 0.4941 mm, 10 faces (baked)
FEATURE [Part::Feature] Part__Feature132  label="Z_-14121C_ZH-14121C-003"
  shape: bbox 398.3 x 44.08 x 358.3 mm, 1962 faces (baked)
FEATURE [Part::Feature] Part__Feature133  label="ZH-1412G001"
  Placement = pos=(0,0.635,0) rot=(0,0,1;0rad)
  shape: bbox 383.7 x 6.35 x 332.9 mm, 136 faces (baked)
FEATURE [Part::Feature] Part__Feature134  label="ZH-95P_DEFAULT036"
  Placement = pos=(-180.594,11.2268,-155.194) rot=(0,0,1;0rad)
  shape: bbox 8.798 x 6.858 x 8.798 mm, 18 faces (baked)
FEATURE [Part::Feature] Part__Feature135  label="ZH-95P_DEFAULT037"
  Placement = pos=(-180.594,11.2268,-155.194) rot=(0,0,1;0rad)
  shape: bbox 5.931 x 5.698 x 5.931 mm, 154 faces (baked)
FEATURE [Part::Feature] Part__Feature136  label="ZH-01L036"
  shape: bbox 29.67 x 17.48 x 21.58 mm, 95 faces (baked)
FEATURE [Part::Feature] Part__Feature137  label="ZH-01L037"
  Placement = pos=(-3.70922,6.42042,-3.4844) rot=(0,0,1;0rad)
  shape: bbox 38.59 x 15.52 x 29.83 mm, 54 faces (baked)
FEATURE [Part::Feature] Part__Feature138  label="ZH-01L038"
  Placement = pos=(-3.88382,6.40232,-3.4844) rot=(0,0,-1;0.101263rad)
  shape: bbox 5.485 x 8.951 x 26.42 mm, 8 faces (baked)
FEATURE [Part::Feature] Part__Feature139  label="ZH-01L039"
  Placement = pos=(-8.2343,12.9933,-3.4844) rot=(0,0,1;1.04312rad)
  shape: bbox 6.537 x 9.263 x 29.53 mm, 8 faces (baked)
FEATURE [Part::Feature] Part__Feature140  label="ZH-01L040"
  Placement = pos=(-3.70922,6.42042,-3.4844) rot=(0,0,1;0rad)
  shape: bbox 46.02 x 13.5 x 24.63 mm, 70 faces (baked)
FEATURE [Part::Feature] Part__Feature141  label="ZH-01L041"
  shape: bbox 29.67 x 17.48 x 21.58 mm, 95 faces (baked)
FEATURE [Part::Feature] Part__Feature142  label="ZH-01L042"
  Placement = pos=(-3.70922,6.42042,-3.4844) rot=(0,0,1;0rad)
  shape: bbox 38.59 x 15.52 x 29.83 mm, 54 faces (baked)
FEATURE [Part::Feature] Part__Feature143  label="ZH-01L043"
  Placement = pos=(-3.88382,6.40232,-3.4844) rot=(0,0,-1;0.101263rad)
  shape: bbox 5.485 x 8.951 x 26.42 mm, 8 faces (baked)
FEATURE [Part::Feature] Part__Feature144  label="ZH-01L044"
  Placement = pos=(-8.2343,12.9933,-3.4844) rot=(0,0,1;1.04312rad)
  shape: bbox 6.537 x 9.263 x 29.53 mm, 8 faces (baked)
FEATURE [Part::Feature] Part__Feature145  label="ZH-01L045"
  Placement = pos=(-3.70922,6.42042,-3.4844) rot=(0,0,1;0rad)
  shape: bbox 46.02 x 13.5 x 24.63 mm, 70 faces (baked)
FEATURE [Part::Feature] Part__Feature146  label="ZH-95P_DEFAULT038"
  Placement = pos=(180.594,11.2268,-155.194) rot=(0,0,1;0rad)
  shape: bbox 8.798 x 6.858 x 8.798 mm, 18 faces (baked)
FEATURE [Part::Feature] Part__Feature147  label="ZH-95P_DEFAULT039"
  Placement = pos=(180.594,11.2268,-155.194) rot=(0,0,1;0rad)
  shape: bbox 5.931 x 5.698 x 5.931 mm, 154 faces (baked)
FEATURE [Part::Feature] Part__Feature148  label="ZH-95P_DEFAULT040"
  Placement = pos=(-180.594,11.2268,155.194) rot=(0,0,1;0rad)
  shape: bbox 8.798 x 6.858 x 8.798 mm, 18 faces (baked)
FEATURE [Part::Feature] Part__Feature149  label="ZH-95P_DEFAULT041"
  Placement = pos=(-180.594,11.2268,155.194) rot=(0,0,1;0rad)
  shape: bbox 5.931 x 5.698 x 5.931 mm, 154 faces (baked)
FEATURE [Part::Feature] Part__Feature150  label="ZH-95P_DEFAULT042"
  Placement = pos=(180.594,11.2268,155.194) rot=(0,0,1;0rad)
  shape: bbox 8.798 x 6.858 x 8.798 mm, 18 faces (baked)
FEATURE [Part::Feature] Part__Feature151  label="ZH-95P_DEFAULT043"
  Placement = pos=(180.594,11.2268,155.194) rot=(0,0,1;0rad)
  shape: bbox 5.931 x 5.698 x 5.931 mm, 154 faces (baked)
FEATURE [Part::Feature] Part__Feature152  label="SCREWS-049_SCREWS-053"
  Placement = pos=(-146.05,-157.759,-120.65) rot=(0.57735,0.57735,0.57735;2.0944rad)
  shape: bbox 10.25 x 12.9 x 10.25 mm, 23 faces (baked)
FEATURE [Part::Feature] Part__Feature153  label="SCREWS-049_SCREWS-054"
  Placement = pos=(146.05,-157.759,-120.65) rot=(0.57735,0.57735,0.57735;2.0944rad)
  shape: bbox 10.25 x 12.9 x 10.25 mm, 23 faces (baked)
FEATURE [Part::Feature] Part__Feature154  label="SCREWS-049_SCREWS-055"
  Placement = pos=(-146.05,-157.759,120.65) rot=(0.57735,0.57735,-0.57735;4.18879rad)
  shape: bbox 10.25 x 12.9 x 10.25 mm, 23 faces (baked)
FEATURE [Part::Feature] Part__Feature155  label="SCREWS-049_SCREWS-056"
  Placement = pos=(146.05,-157.759,120.65) rot=(-0.57735,-0.57735,0.57735;2.0944rad)
  shape: bbox 10.25 x 12.9 x 10.25 mm, 23 faces (baked)
FEATURE [App::Part] ZH_01L006  label="ZH-01L046"
  Group = -> [Part__Feature136,Part__Feature137,Part__Feature138,Part__Feature139,Part__Feature140]
  Origin = -> Origin031
  Placement = pos=(-104.648,-7.112,166.624) rot=(0.579853,0.572312,0.579853;2.10197rad)
FEATURE [App::Part] ZH_01L007  label="ZH-01L047"
  Group = -> [Part__Feature141,Part__Feature142,Part__Feature143,Part__Feature144,Part__Feature145]
  Origin = -> Origin032
  Placement = pos=(104.648,-7.112,166.624) rot=(0.579853,0.572312,0.579853;2.10197rad)
FEATURE [App::Part] ZH_95P_DEFAULT012  label="ZH-95P_DEFAULT044"
  Group = -> [Part__Feature134,Part__Feature135]
  Origin = -> Origin030
FEATURE [App::Part] ZH_95P_DEFAULT013  label="ZH-95P_DEFAULT045"
  Group = -> [Part__Feature146,Part__Feature147]
  Origin = -> Origin033
FEATURE [App::Part] ZH_95P_DEFAULT014  label="ZH-95P_DEFAULT046"
  Group = -> [Part__Feature148,Part__Feature149]
  Origin = -> Origin034
FEATURE [App::Part] ZH_95P_DEFAULT015  label="ZH-95P_DEFAULT047"
  Group = -> [Part__Feature150,Part__Feature151]
  Origin = -> Origin035
FEATURE [App::Part] Z__14121CG_ZH_14121CG_003  label="Z_-14121CG_ZH-14121CG-003"
  Group = -> [Part__Feature132,Part__Feature133]
  Origin = -> Origin029
  Placement = pos=(0,0.762,0) rot=(0,0,1;0rad)
FEATURE [App::Part] Z__14126BI_ZH_14126BI_002  label="Z_-14126BI_ZH-14126BI-002"
  Group = -> [Part__Feature118,Part__Feature119,Part__Feature120,Part__Feature121,Part__Feature122,Part__Feature123,Part__Feature124,Part__Feature125,Part__Feature126,Part__Feature127,Part__Feature128,Part__Feature129,Part__Feature130,Part__Feature131]
  Origin = -> Origin037
FEATURE [App::Part] ZH_141206_093  label="ZH-141206-093"
  Group = -> [Z__14126BI_ZH_14126BI_002,Z__14121CG_ZH_14121CG_003,ZH_95P_DEFAULT012,ZH_01L006,ZH_01L007,ZH_95P_DEFAULT013,ZH_95P_DEFAULT014,ZH_95P_DEFAULT015,Part__Feature152,Part__Feature153,Part__Feature154,Part__Feature155]
  Origin = -> Origin036
  Placement = pos=(370,670,163) rot=(0,0.707107,0.707107;3.14159rad)
FEATURE [Part::Feature] Part__Feature156  label="3201T45_Black-Oxide Steel U-Bolt"
  Placement = pos=(1050,152.5,2.67e-13) rot=(0.57735,0.57735,0.57735;2.0944rad)
  shape: bbox 19.05 x 36.51 x 39.69 mm, 130 faces (baked)
FEATURE [Part::Feature] Part__Feature157  label="3201T45_Black-Oxide Steel U-Bolt001"
  Placement = pos=(1050,542.5,2.67e-13) rot=(0.57735,0.57735,0.57735;2.0944rad)
  shape: bbox 19.05 x 36.51 x 39.69 mm, 130 faces (baked)
FEATURE [Part::Feature] Part__Feature158  label="3201T45_Black-Oxide Steel U-Bolt002"
  Placement = pos=(1050,412.5,2.67e-13) rot=(0.57735,0.57735,0.57735;2.0944rad)
  shape: bbox 19.05 x 36.51 x 39.69 mm, 130 faces (baked)
FEATURE [Part::Feature] Part__Feature159  label="3201T45_Black-Oxide Steel U-Bolt003"
  Placement = pos=(1050,802.5,2.67e-13) rot=(0.57735,0.57735,0.57735;2.0944rad)
  shape: bbox 19.05 x 36.51 x 39.69 mm, 130 faces (baked)
FEATURE [Part::Feature] Part__Feature160  label="3201T45_Black-Oxide Steel U-Bolt004"
  Placement = pos=(409,110,2.67e-13) rot=(1,0,0;1.5708rad)
  shape: bbox 36.51 x 19.05 x 39.69 mm, 130 faces (baked)
FEATURE [Part::Feature] Part__Feature161  label="3201T45_Black-Oxide Steel U-Bolt005"
  Placement = pos=(579,120,2.67e-13) rot=(1,0,0;1.5708rad)
  shape: bbox 36.51 x 19.05 x 39.69 mm, 130 faces (baked)
FEATURE [Part::Feature] Part__Feature162  label="3201T45_Black-Oxide Steel U-Bolt006"
  Placement = pos=(409,845,2.67e-13) rot=(1,0,0;1.5708rad)
  shape: bbox 36.51 x 19.05 x 39.69 mm, 130 faces (baked)
FEATURE [Part::Feature] Part__Feature163  label="3201T45_Black-Oxide Steel U-Bolt007"
  Placement = pos=(579,845,2.67e-13) rot=(1,0,0;1.5708rad)
  shape: bbox 36.51 x 19.05 x 39.69 mm, 130 faces (baked)
FEATURE [Part::Feature] Part__Feature164  label="3201T45_Black-Oxide Steel U-Bolt008"
  Placement = pos=(170,152.5,2.67e-13) rot=(0.57735,0.57735,0.57735;2.0944rad)
  shape: bbox 19.05 x 36.51 x 39.69 mm, 130 faces (baked)
FEATURE [Part::Feature] Part__Feature165  label="3201T45_Black-Oxide Steel U-Bolt009"
  Placement = pos=(170,412.5,2.67e-13) rot=(0.57735,0.57735,0.57735;2.0944rad)
  shape: bbox 19.05 x 36.51 x 39.69 mm, 130 faces (baked)
FEATURE [Part::Feature] Part__Feature166  label="3201T45_Black-Oxide Steel U-Bolt010"
  Placement = pos=(170,542.5,2.67e-13) rot=(0.57735,0.57735,0.57735;2.0944rad)
  shape: bbox 19.05 x 36.51 x 39.69 mm, 130 faces (baked)
FEATURE [Part::Feature] Part__Feature167  label="3201T45_Black-Oxide Steel U-Bolt011"
  Placement = pos=(170,802.5,2.67e-13) rot=(0.57735,0.57735,0.57735;2.0944rad)
  shape: bbox 19.05 x 36.51 x 39.69 mm, 130 faces (baked)
FEATURE [Part::MultiFuse] Fusion008  label="UBolts"
  Shapes = -> [Part__Feature156,Part__Feature157,Part__Feature158,Part__Feature159,Part__Feature160,Part__Feature161,Part__Feature162,Part__Feature163,Part__Feature164,Part__Feature165,Part__Feature166,Part__Feature167]
FEATURE [Part::Feature] Part__Feature168  label="3201T45_Black-Oxide Steel U-Bolt012"
  Placement = pos=(1050,152.5,2.67e-13) rot=(0.57735,0.57735,0.57735;2.0944rad)
  shape: bbox 19.05 x 36.51 x 39.69 mm, 130 faces (baked)
FEATURE [Part::Feature] Part__Feature169  label="3201T45_Black-Oxide Steel U-Bolt013"
  Placement = pos=(1050,542.5,2.67e-13) rot=(0.57735,0.57735,0.57735;2.0944rad)
  shape: bbox 19.05 x 36.51 x 39.69 mm, 130 faces (baked)
FEATURE [Part::Feature] Part__Feature170  label="3201T45_Black-Oxide Steel U-Bolt014"
  Placement = pos=(1050,412.5,2.67e-13) rot=(0.57735,0.57735,0.57735;2.0944rad)
  shape: bbox 19.05 x 36.51 x 39.69 mm, 130 faces (baked)
FEATURE [Part::Feature] Part__Feature171  label="3201T45_Black-Oxide Steel U-Bolt015"
  Placement = pos=(1050,802.5,2.67e-13) rot=(0.57735,0.57735,0.57735;2.0944rad)
  shape: bbox 19.05 x 36.51 x 39.69 mm, 130 faces (baked)
FEATURE [Part::Feature] Part__Feature172  label="3201T45_Black-Oxide Steel U-Bolt016"
  Placement = pos=(409,110,2.67e-13) rot=(1,0,0;1.5708rad)
  shape: bbox 36.51 x 19.05 x 39.69 mm, 130 faces (baked)
FEATURE [Part::Feature] Part__Feature173  label="3201T45_Black-Oxide Steel U-Bolt017"
  Placement = pos=(579,120,2.67e-13) rot=(1,0,0;1.5708rad)
  shape: bbox 36.51 x 19.05 x 39.69 mm, 130 faces (baked)
FEATURE [Part::Feature] Part__Feature174  label="3201T45_Black-Oxide Steel U-Bolt018"
  Placement = pos=(409,845,2.67e-13) rot=(1,0,0;1.5708rad)
  shape: bbox 36.51 x 19.05 x 39.69 mm, 130 faces (baked)
FEATURE [Part::Feature] Part__Feature175  label="3201T45_Black-Oxide Steel U-Bolt019"
  Placement = pos=(579,845,2.67e-13) rot=(1,0,0;1.5708rad)
  shape: bbox 36.51 x 19.05 x 39.69 mm, 130 faces (baked)
FEATURE [Part::Feature] Part__Feature176  label="3201T45_Black-Oxide Steel U-Bolt020"
  Placement = pos=(170,152.5,2.67e-13) rot=(0.57735,0.57735,0.57735;2.0944rad)
  shape: bbox 19.05 x 36.51 x 39.69 mm, 130 faces (baked)
FEATURE [Part::Feature] Part__Feature177  label="3201T45_Black-Oxide Steel U-Bolt021"
  Placement = pos=(170,412.5,2.67e-13) rot=(0.57735,0.57735,0.57735;2.0944rad)
  shape: bbox 19.05 x 36.51 x 39.69 mm, 130 faces (baked)
FEATURE [Part::Feature] Part__Feature178  label="3201T45_Black-Oxide Steel U-Bolt022"
  Placement = pos=(170,542.5,2.67e-13) rot=(0.57735,0.57735,0.57735;2.0944rad)
  shape: bbox 19.05 x 36.51 x 39.69 mm, 130 faces (baked)
FEATURE [Part::Feature] Part__Feature179  label="3201T45_Black-Oxide Steel U-Bolt023"
  Placement = pos=(170,802.5,2.67e-13) rot=(0.57735,0.57735,0.57735;2.0944rad)
  shape: bbox 19.05 x 36.51 x 39.69 mm, 130 faces (baked)
FEATURE [Part::MultiFuse] Fusion009  label="UBolts001"
  Placement = pos=(0,0,7) rot=(0,0,1;0rad)
  Shapes = -> [Part__Feature168,Part__Feature169,Part__Feature170,Part__Feature171,Part__Feature172,Part__Feature173,Part__Feature174,Part__Feature175,Part__Feature176,Part__Feature177,Part__Feature178,Part__Feature179]
FEATURE [Part::Cut] Cut  label="Aluminum_sheet_cut"
  Base = -> Box
  Tool = -> Fusion009
FEATURE [Part::Cylinder] Cylinder053
  Angle = 360
  AttacherType = Attacher::AttachEngine3D
  FirstAngle = 0
  Height = 30
  Placement = pos=(1050.01,142.17,-5) rot=(0,0,1;0rad)
  Radius = 3.25
  SecondAngle = 0
FEATURE [Part::Cylinder] Cylinder054
  Angle = 360
  AttacherType = Attacher::AttachEngine3D
  FirstAngle = 0
  Height = 30
  Placement = pos=(1050.01,162.8,-5) rot=(0,0,1;0rad)
  Radius = 3.25
  SecondAngle = 0
FEATURE [Part::Cylinder] Cylinder055
  Angle = 360
  AttacherType = Attacher::AttachEngine3D
  FirstAngle = 0
  Height = 30
  Placement = pos=(1050.01,402.17,-5) rot=(0,0,1;0rad)
  Radius = 3.25
  SecondAngle = 0
FEATURE [Part::Cylinder] Cylinder056
  Angle = 360
  AttacherType = Attacher::AttachEngine3D
  FirstAngle = 0
  Height = 30
  Placement = pos=(1050.01,422.8,-5) rot=(0,0,1;0rad)
  Radius = 3.25
  SecondAngle = 0
FEATURE [Part::Cylinder] Cylinder057
  Angle = 360
  AttacherType = Attacher::AttachEngine3D
  FirstAngle = 0
  Height = 30
  Placement = pos=(1050.01,532.17,-5) rot=(0,0,1;0rad)
  Radius = 3.25
  SecondAngle = 0
FEATURE [Part::Cylinder] Cylinder058
  Angle = 360
  AttacherType = Attacher::AttachEngine3D
  FirstAngle = 0
  Height = 30
  Placement = pos=(1050.01,552.8,-5) rot=(0,0,1;0rad)
  Radius = 3.25
  SecondAngle = 0
FEATURE [Part::Cylinder] Cylinder059
  Angle = 360
  AttacherType = Attacher::AttachEngine3D
  FirstAngle = 0
  Height = 30
  Placement = pos=(1050.01,792.17,-5) rot=(0,0,1;0rad)
  Radius = 3.25
  SecondAngle = 0
FEATURE [Part::Cylinder] Cylinder060
  Angle = 360
  AttacherType = Attacher::AttachEngine3D
  FirstAngle = 0
  Height = 30
  Placement = pos=(1050.01,812.8,-5) rot=(0,0,1;0rad)
  Radius = 3.25
  SecondAngle = 0
FEATURE [Part::Cylinder] Cylinder061
  Angle = 360
  AttacherType = Attacher::AttachEngine3D
  FirstAngle = 0
  Height = 30
  Placement = pos=(589.31,845,-5) rot=(0,0,1;0rad)
  Radius = 3.25
  SecondAngle = 0
FEATURE [Part::Cylinder] Cylinder062
  Angle = 360
  AttacherType = Attacher::AttachEngine3D
  FirstAngle = 0
  Height = 30
  Placement = pos=(568.68,845,-5) rot=(0,0,1;0rad)
  Radius = 3.25
  SecondAngle = 0
FEATURE [Part::Cylinder] Cylinder063
  Angle = 360
  AttacherType = Attacher::AttachEngine3D
  FirstAngle = 0
  Height = 30
  Placement = pos=(419.31,845,-5) rot=(0,0,1;0rad)
  Radius = 3.25
  SecondAngle = 0
FEATURE [Part::Cylinder] Cylinder064
  Angle = 360
  AttacherType = Attacher::AttachEngine3D
  FirstAngle = 0
  Height = 30
  Placement = pos=(398.68,845,-5) rot=(0,0,1;0rad)
  Radius = 3.25
  SecondAngle = 0
FEATURE [Part::Cylinder] Cylinder065
  Angle = 360
  AttacherType = Attacher::AttachEngine3D
  FirstAngle = 0
  Height = 30
  Placement = pos=(589.31,120,-5) rot=(0,0,1;0rad)
  Radius = 3.25
  SecondAngle = 0
FEATURE [Part::Cylinder] Cylinder066
  Angle = 360
  AttacherType = Attacher::AttachEngine3D
  FirstAngle = 0
  Height = 30
  Placement = pos=(568.68,120,-5) rot=(0,0,1;0rad)
  Radius = 3.25
  SecondAngle = 0
FEATURE [Part::Cylinder] Cylinder067
  Angle = 360
  AttacherType = Attacher::AttachEngine3D
  FirstAngle = 0
  Height = 30
  Placement = pos=(419.31,110,-5) rot=(0,0,1;0rad)
  Radius = 3.25
  SecondAngle = 0
FEATURE [Part::Cylinder] Cylinder068
  Angle = 360
  AttacherType = Attacher::AttachEngine3D
  FirstAngle = 0
  Height = 30
  Placement = pos=(398.68,110,-5) rot=(0,0,1;0rad)
  Radius = 3.25
  SecondAngle = 0
FEATURE [Part::Cylinder] Cylinder069
  Angle = 360
  AttacherType = Attacher::AttachEngine3D
  FirstAngle = 0
  Height = 30
  Placement = pos=(170.01,142.17,-5) rot=(0,0,1;0rad)
  Radius = 3.25
  SecondAngle = 0
FEATURE [Part::Cylinder] Cylinder070
  Angle = 360
  AttacherType = Attacher::AttachEngine3D
  FirstAngle = 0
  Height = 30
  Placement = pos=(170.01,162.8,-5) rot=(0,0,1;0rad)
  Radius = 3.25
  SecondAngle = 0
FEATURE [Part::Cylinder] Cylinder071
  Angle = 360
  AttacherType = Attacher::AttachEngine3D
  FirstAngle = 0
  Height = 30
  Placement = pos=(170.01,402.17,-5) rot=(0,0,1;0rad)
  Radius = 3.25
  SecondAngle = 0
FEATURE [Part::Cylinder] Cylinder072
  Angle = 360
  AttacherType = Attacher::AttachEngine3D
  FirstAngle = 0
  Height = 30
  Placement = pos=(170.01,422.8,-5) rot=(0,0,1;0rad)
  Radius = 3.25
  SecondAngle = 0
FEATURE [Part::Cylinder] Cylinder073
  Angle = 360
  AttacherType = Attacher::AttachEngine3D
  FirstAngle = 0
  Height = 30
  Placement = pos=(170.01,532.17,-5) rot=(0,0,1;0rad)
  Radius = 3.25
  SecondAngle = 0
FEATURE [Part::Cylinder] Cylinder074
  Angle = 360
  AttacherType = Attacher::AttachEngine3D
  FirstAngle = 0
  Height = 30
  Placement = pos=(170.01,552.8,-5) rot=(0,0,1;0rad)
  Radius = 3.25
  SecondAngle = 0
FEATURE [Part::Cylinder] Cylinder075
  Angle = 360
  AttacherType = Attacher::AttachEngine3D
  FirstAngle = 0
  Height = 30
  Placement = pos=(170.01,792.17,-5) rot=(0,0,1;0rad)
  Radius = 3.25
  SecondAngle = 0
FEATURE [Part::Cylinder] Cylinder076
  Angle = 360
  AttacherType = Attacher::AttachEngine3D
  FirstAngle = 0
  Height = 30
  Placement = pos=(170.01,812.8,-5) rot=(0,0,1;0rad)
  Radius = 3.25
  SecondAngle = 0
FEATURE [Part::MultiFuse] Fusion010  label="Cylinders"
  Shapes = -> [Cylinder053,Cylinder054,Cylinder055,Cylinder056,Cylinder057,Cylinder058,Cylinder059,Cylinder060,Cylinder061,Cylinder062,Cylinder063,Cylinder064,Cylinder065,Cylinder066,Cylinder067,Cylinder068,Cylinder069,Cylinder070,Cylinder071,Cylinder072,Cylinder073,Cylinder074,Cylinder075,Cylinder076]
FEATURE [Part::Cut] Cut001  label="Aluminum_Cut"
  Base = -> Cut
  Tool = -> Fusion010
FEATURE [Part::MultiFuse] Fusion011  label="Car_frame"
  Shapes = -> [Fusion,Fusion001,Fusion002,Fusion003,Fusion004,Fusion005,Fusion006,Fusion007]
FEATURE [App::Part] Part  label="Car_mount"
  Group = -> [Part__Feature169,Part__Feature168,Part__Feature174,Part__Feature170,Part__Feature176,Part__Feature179,Part__Feature171,Part__Feature178,Part__Feature175,Part__Feature172,Part__Feature173,Part__Feature177,Fusion009,Fusion010,Cut,Cylinder072,Cylinder056,Cylinder059,Cylinder055,Cylinder053,Cylinder067,Cylinder054,Cylinder057,Cylinder058,Cylinder075,Cylinder062,Cylinder065,Cylinder066,Cylinder063,+76 more]
  Origin = -> Origin
FEATURE [Part::Box] Box001  label="Cube001"
  AttacherType = Attacher::AttachEngine3D
  Height = 3.25
  Length = 762
  Placement = pos=(1065,96,7) rot=(0,0,1;1.5708rad)
  Width = 914.4
FEATURE [Part::Cylinder] Cylinder077
  Angle = 360
  AttacherType = Attacher::AttachEngine3D
  FirstAngle = 0
  Height = 30
  Placement = pos=(1050.01,142.17,-5) rot=(0,0,1;0rad)
  Radius = 3.25
  SecondAngle = 0
FEATURE [Part::Cylinder] Cylinder078
  Angle = 360
  AttacherType = Attacher::AttachEngine3D
  FirstAngle = 0
  Height = 30
  Placement = pos=(1050.01,162.8,-5) rot=(0,0,1;0rad)
  Radius = 3.25
  SecondAngle = 0
FEATURE [Part::Cylinder] Cylinder079
  Angle = 360
  AttacherType = Attacher::AttachEngine3D
  FirstAngle = 0
  Height = 30
  Placement = pos=(1050.01,402.17,-5) rot=(0,0,1;0rad)
  Radius = 3.25
  SecondAngle = 0
FEATURE [Part::Cylinder] Cylinder080
  Angle = 360
  AttacherType = Attacher::AttachEngine3D
  FirstAngle = 0
  Height = 30
  Placement = pos=(1050.01,422.8,-5) rot=(0,0,1;0rad)
  Radius = 3.25
  SecondAngle = 0
FEATURE [Part::Cylinder] Cylinder081
  Angle = 360
  AttacherType = Attacher::AttachEngine3D
  FirstAngle = 0
  Height = 30
  Placement = pos=(1050.01,532.17,-5) rot=(0,0,1;0rad)
  Radius = 3.25
  SecondAngle = 0
FEATURE [Part::Cylinder] Cylinder082
  Angle = 360
  AttacherType = Attacher::AttachEngine3D
  FirstAngle = 0
  Height = 30
  Placement = pos=(1050.01,552.8,-5) rot=(0,0,1;0rad)
  Radius = 3.25
  SecondAngle = 0
FEATURE [Part::Cylinder] Cylinder083
  Angle = 360
  AttacherType = Attacher::AttachEngine3D
  FirstAngle = 0
  Height = 30
  Placement = pos=(1050.01,792.17,-5) rot=(0,0,1;0rad)
  Radius = 3.25
  SecondAngle = 0
FEATURE [Part::Cylinder] Cylinder084
  Angle = 360
  AttacherType = Attacher::AttachEngine3D
  FirstAngle = 0
  Height = 30
  Placement = pos=(1050.01,812.8,-5) rot=(0,0,1;0rad)
  Radius = 3.25
  SecondAngle = 0
FEATURE [Part::Cylinder] Cylinder085
  Angle = 360
  AttacherType = Attacher::AttachEngine3D
  FirstAngle = 0
  Height = 30
  Placement = pos=(589.31,845,-5) rot=(0,0,1;0rad)
  Radius = 3.25
  SecondAngle = 0
FEATURE [Part::Cylinder] Cylinder086
  Angle = 360
  AttacherType = Attacher::AttachEngine3D
  FirstAngle = 0
  Height = 30
  Placement = pos=(568.68,845,-5) rot=(0,0,1;0rad)
  Radius = 3.25
  SecondAngle = 0
FEATURE [Part::Cylinder] Cylinder087
  Angle = 360
  AttacherType = Attacher::AttachEngine3D
  FirstAngle = 0
  Height = 30
  Placement = pos=(419.31,845,-5) rot=(0,0,1;0rad)
  Radius = 3.25
  SecondAngle = 0
FEATURE [Part::Cylinder] Cylinder088
  Angle = 360
  AttacherType = Attacher::AttachEngine3D
  FirstAngle = 0
  Height = 30
  Placement = pos=(398.68,845,-5) rot=(0,0,1;0rad)
  Radius = 3.25
  SecondAngle = 0
FEATURE [Part::Cylinder] Cylinder089
  Angle = 360
  AttacherType = Attacher::AttachEngine3D
  FirstAngle = 0
  Height = 30
  Placement = pos=(589.31,120,-5) rot=(0,0,1;0rad)
  Radius = 3.25
  SecondAngle = 0
FEATURE [Part::Cylinder] Cylinder090
  Angle = 360
  AttacherType = Attacher::AttachEngine3D
  FirstAngle = 0
  Height = 30
  Placement = pos=(568.68,120,-5) rot=(0,0,1;0rad)
  Radius = 3.25
  SecondAngle = 0
FEATURE [Part::Cylinder] Cylinder091
  Angle = 360
  AttacherType = Attacher::AttachEngine3D
  FirstAngle = 0
  Height = 30
  Placement = pos=(419.31,110,-5) rot=(0,0,1;0rad)
  Radius = 3.25
  SecondAngle = 0
FEATURE [Part::Cylinder] Cylinder092
  Angle = 360
  AttacherType = Attacher::AttachEngine3D
  FirstAngle = 0
  Height = 30
  Placement = pos=(398.68,110,-5) rot=(0,0,1;0rad)
  Radius = 3.25
  SecondAngle = 0
FEATURE [Part::Cylinder] Cylinder093
  Angle = 360
  AttacherType = Attacher::AttachEngine3D
  FirstAngle = 0
  Height = 30
  Placement = pos=(170.01,142.17,-5) rot=(0,0,1;0rad)
  Radius = 3.25
  SecondAngle = 0
FEATURE [Part::Cylinder] Cylinder094
  Angle = 360
  AttacherType = Attacher::AttachEngine3D
  FirstAngle = 0
  Height = 30
  Placement = pos=(170.01,162.8,-5) rot=(0,0,1;0rad)
  Radius = 3.25
  SecondAngle = 0
FEATURE [Part::Cylinder] Cylinder095
  Angle = 360
  AttacherType = Attacher::AttachEngine3D
  FirstAngle = 0
  Height = 30
  Placement = pos=(170.01,402.17,-5) rot=(0,0,1;0rad)
  Radius = 3.25
  SecondAngle = 0
FEATURE [Part::Cylinder] Cylinder096
  Angle = 360
  AttacherType = Attacher::AttachEngine3D
  FirstAngle = 0
  Height = 30
  Placement = pos=(170.01,422.8,-5) rot=(0,0,1;0rad)
  Radius = 3.25
  SecondAngle = 0
FEATURE [Part::Cylinder] Cylinder097
  Angle = 360
  AttacherType = Attacher::AttachEngine3D
  FirstAngle = 0
  Height = 30
  Placement = pos=(170.01,532.17,-5) rot=(0,0,1;0rad)
  Radius = 3.25
  SecondAngle = 0
FEATURE [Part::Cylinder] Cylinder098
  Angle = 360
  AttacherType = Attacher::AttachEngine3D
  FirstAngle = 0
  Height = 30
  Placement = pos=(170.01,552.8,-5) rot=(0,0,1;0rad)
  Radius = 3.25
  SecondAngle = 0
FEATURE [Part::Cylinder] Cylinder099
  Angle = 360
  AttacherType = Attacher::AttachEngine3D
  FirstAngle = 0
  Height = 30
  Placement = pos=(170.01,792.17,-5) rot=(0,0,1;0rad)
  Radius = 3.25
  SecondAngle = 0
FEATURE [Part::Cylinder] Cylinder100
  Angle = 360
  AttacherType = Attacher::AttachEngine3D
  FirstAngle = 0
  Height = 30
  Placement = pos=(170.01,812.8,-5) rot=(0,0,1;0rad)
  Radius = 3.25
  SecondAngle = 0
FEATURE [Part::MultiFuse] Fusion013  label="Cylinders001"
  Shapes = -> [Cylinder077,Cylinder078,Cylinder079,Cylinder080,Cylinder081,Cylinder082,Cylinder083,Cylinder084,Cylinder085,Cylinder086,Cylinder087,Cylinder088,Cylinder089,Cylinder090,Cylinder091,Cylinder092,Cylinder093,Cylinder094,Cylinder095,Cylinder096,Cylinder097,Cylinder098,Cylinder099,Cylinder100]
FEATURE [Part::Feature] Part__Feature180  label="3201T45_Black-Oxide Steel U-Bolt024"
  Placement = pos=(1050,152.5,2.67e-13) rot=(0.57735,0.57735,0.57735;2.0944rad)
  shape: bbox 19.05 x 36.51 x 39.69 mm, 130 faces (baked)
FEATURE [Part::Feature] Part__Feature181  label="3201T45_Black-Oxide Steel U-Bolt025"
  Placement = pos=(1050,542.5,2.67e-13) rot=(0.57735,0.57735,0.57735;2.0944rad)
  shape: bbox 19.05 x 36.51 x 39.69 mm, 130 faces (baked)
FEATURE [Part::Feature] Part__Feature182  label="3201T45_Black-Oxide Steel U-Bolt026"
  Placement = pos=(1050,412.5,2.67e-13) rot=(0.57735,0.57735,0.57735;2.0944rad)
  shape: bbox 19.05 x 36.51 x 39.69 mm, 130 faces (baked)
FEATURE [Part::Feature] Part__Feature183  label="3201T45_Black-Oxide Steel U-Bolt027"
  Placement = pos=(1050,802.5,2.67e-13) rot=(0.57735,0.57735,0.57735;2.0944rad)
  shape: bbox 19.05 x 36.51 x 39.69 mm, 130 faces (baked)
FEATURE [Part::Feature] Part__Feature184  label="3201T45_Black-Oxide Steel U-Bolt028"
  Placement = pos=(409,110,2.67e-13) rot=(1,0,0;1.5708rad)
  shape: bbox 36.51 x 19.05 x 39.69 mm, 130 faces (baked)
FEATURE [Part::Feature] Part__Feature185  label="3201T45_Black-Oxide Steel U-Bolt029"
  Placement = pos=(579,120,2.67e-13) rot=(1,0,0;1.5708rad)
  shape: bbox 36.51 x 19.05 x 39.69 mm, 130 faces (baked)
FEATURE [Part::Feature] Part__Feature186  label="3201T45_Black-Oxide Steel U-Bolt030"
  Placement = pos=(409,845,2.67e-13) rot=(1,0,0;1.5708rad)
  shape: bbox 36.51 x 19.05 x 39.69 mm, 130 faces (baked)
FEATURE [Part::Feature] Part__Feature187  label="3201T45_Black-Oxide Steel U-Bolt031"
  Placement = pos=(579,845,2.67e-13) rot=(1,0,0;1.5708rad)
  shape: bbox 36.51 x 19.05 x 39.69 mm, 130 faces (baked)
FEATURE [Part::Feature] Part__Feature188  label="3201T45_Black-Oxide Steel U-Bolt032"
  Placement = pos=(170,152.5,2.67e-13) rot=(0.57735,0.57735,0.57735;2.0944rad)
  shape: bbox 19.05 x 36.51 x 39.69 mm, 130 faces (baked)
FEATURE [Part::Feature] Part__Feature189  label="3201T45_Black-Oxide Steel U-Bolt033"
  Placement = pos=(170,412.5,2.67e-13) rot=(0.57735,0.57735,0.57735;2.0944rad)
  shape: bbox 19.05 x 36.51 x 39.69 mm, 130 faces (baked)
FEATURE [Part::Feature] Part__Feature190  label="3201T45_Black-Oxide Steel U-Bolt034"
  Placement = pos=(170,542.5,2.67e-13) rot=(0.57735,0.57735,0.57735;2.0944rad)
  shape: bbox 19.05 x 36.51 x 39.69 mm, 130 faces (baked)
FEATURE [Part::Feature] Part__Feature191  label="3201T45_Black-Oxide Steel U-Bolt035"
  Placement = pos=(170,802.5,2.67e-13) rot=(0.57735,0.57735,0.57735;2.0944rad)
  shape: bbox 19.05 x 36.51 x 39.69 mm, 130 faces (baked)
FEATURE [Part::MultiFuse] Fusion012  label="UBolts002"
  Placement = pos=(0,0,7) rot=(0,0,1;0rad)
  Shapes = -> [Part__Feature180,Part__Feature181,Part__Feature182,Part__Feature183,Part__Feature184,Part__Feature185,Part__Feature186,Part__Feature187,Part__Feature188,Part__Feature189,Part__Feature190,Part__Feature191]
FEATURE [Part::Cut] Cut002  label="Aluminum_sheet_cut001"
  Base = -> Box001
  Tool = -> Fusion012
FEATURE [Part::Cut] Cut003  label="Aluminum_Cut001"
  Base = -> Cut002
  Placement = pos=(0,0,0) rot=(0,0,-1;1.5708rad)
  Tool = -> Fusion013
FEATURE [TechDraw::DrawSVGTemplate] Template
  Height = 841
  Orientation = 1
  Template = C:/Program Files/FreeCAD 0.21/data/Mod/TechDraw/Templates/A0_Landscape_blank.svg
  Width = 1189
FEATURE [TechDraw::DrawViewPart] View
  CoarseView = false
  Direction = (0,0,1)
  Focus = 100
  HardHidden = false
  IsoCount = 0
  IsoHidden = false
  IsoVisible = false
  LockPosition = false
  Perspective = false
  Rotation = 0
  ScaleType = 0
  ScrubCount = 0
  SeamHidden = false
  SeamVisible = false
  SmoothHidden = false
  SmoothVisible = true
  Source = -> [Cut003]
  X = 594.5
  XDirection = (0,-1,0)
  Y = 420.5
FEATURE [TechDraw::DrawViewDimension] Dimension
  AngleOverride = false
  Arbitrary = false
  ArbitraryTolerances = false
  EqualTolerance = true
  ExtensionAngle = 0
  FormatSpec = ⌀%.2w
  FormatSpecOverTolerance = %+.2w
  FormatSpecUnderTolerance = %+.2w
  Inverted = false
  LineAngle = 0
  LockPosition = false
  MeasureType = 1
  OverTolerance = 0
  References2D = -> [View]
  Rotation = 0
  ScaleType = 0
  TheoreticalExact = false
  Type = 5
  UnderTolerance = 0
  X = -407.5
  Y = 343.25
FEATURE [TechDraw::DrawPage] Page
  KeepUpdated = true
  NextBalloonIndex = 1
  ProjectionType = 0
  Template = -> Template
  Views = -> [View,Dimension]
FEATURE [Part::Box] Box202  label="Cube202"
  AttacherType = Attacher::AttachEngine3D
  Height = 50
  Length = 60
  Placement = pos=(-450,39,25) rot=(0,0,1;0rad)
  Width = 90
FEATURE [Part::Box] Box203  label="Cube203"
  AttacherType = Attacher::AttachEngine3D
  Height = 46
  Length = 50
  Placement = pos=(-445,44,30) rot=(0,0,1;0rad)
  Width = 80
FEATURE [Part::Box] Box204  label="Cube204"
  AttacherType = Attacher::AttachEngine3D
  Height = 4
  Length = 5
  Placement = pos=(-421,118,61) rot=(0,0,1;0rad)
  Width = 6
FEATURE [Part::Box] Box205  label="Cube205"
  AttacherType = Attacher::AttachEngine3D
  Height = 4
  Length = 5
  Placement = pos=(-400,118,61) rot=(0,0,1;0rad)
  Width = 6
FEATURE [Part::Box] Box206  label="Cube206"
  AttacherType = Attacher::AttachEngine3D
  Height = 4
  Length = 6
  Placement = pos=(-401,98,61) rot=(0,0,1;0rad)
  Width = 5
FEATURE [Part::Box] Box207  label="Cube207"
  AttacherType = Attacher::AttachEngine3D
  Height = 12
  Length = 10
  Placement = pos=(-425,84,13) rot=(0,0,1;0rad)
  Width = 6.5
FEATURE [Part::Box] Box208  label="Cube208"
  AttacherType = Attacher::AttachEngine3D
  Height = 5.5
  Length = 10
  Placement = pos=(-425,93.5,19) rot=(1,0,0;1.5708rad)
  Width = 6
FEATURE [Part::Box] Box209  label="Cube209"
  AttacherType = Attacher::AttachEngine3D
  Height = 5.5
  Length = 10
  Placement = pos=(-425,119.5,19) rot=(1,0,0;1.5708rad)
  Width = 6
FEATURE [Part::Box] Box210  label="Cube210"
  AttacherType = Attacher::AttachEngine3D
  Height = 12
  Length = 10
  Placement = pos=(-425,117,13) rot=(0,0,1;0rad)
  Width = 6.5
FEATURE [Part::Box] Box211  label="Cube211"
  AttacherType = Attacher::AttachEngine3D
  Height = 12
  Length = 10
  Placement = pos=(-425,84,13) rot=(0,0,1;0rad)
  Width = 6.5
FEATURE [Part::Box] Box212  label="Cube212"
  AttacherType = Attacher::AttachEngine3D
  Height = 5.5
  Length = 10
  Placement = pos=(-425,93.5,19) rot=(1,0,0;1.5708rad)
  Width = 6
FEATURE [Part::Box] Box213  label="Cube213"
  AttacherType = Attacher::AttachEngine3D
  Height = 5.5
  Length = 10
  Placement = pos=(-425,119.5,19) rot=(1,0,0;1.5708rad)
  Width = 6
FEATURE [Part::Box] Box214  label="Cube214"
  AttacherType = Attacher::AttachEngine3D
  Height = 12
  Length = 10
  Placement = pos=(-425,117,13) rot=(0,0,1;0rad)
  Width = 6.5
FEATURE [Part::Cut] Cut011
  Base = -> Box202
  Tool = -> Box203
FEATURE [Part::Cylinder] Cylinder101
  Angle = 360
  AttacherType = Attacher::AttachEngine3D
  FirstAngle = 0
  Height = 15
  Placement = pos=(-47.7,61,61.5) rot=(0,0,1;0rad)
  Radius = 3
  SecondAngle = 0
FEATURE [Part::Cylinder] Cylinder102
  Angle = 360
  AttacherType = Attacher::AttachEngine3D
  FirstAngle = 0
  Height = 15
  Placement = pos=(-79.3,61,61.5) rot=(0,0,1;0rad)
  Radius = 3
  SecondAngle = 0
FEATURE [Part::Cylinder] Cylinder103
  Angle = 360
  AttacherType = Attacher::AttachEngine3D
  FirstAngle = 0
  Height = 15
  Placement = pos=(-47.7,61,61.5) rot=(0,0,1;0rad)
  Radius = 3
  SecondAngle = 0
FEATURE [Part::Cylinder] Cylinder104
  Angle = 360
  AttacherType = Attacher::AttachEngine3D
  FirstAngle = 0
  Height = 15
  Placement = pos=(-79.3,61,61.5) rot=(0,0,1;0rad)
  Radius = 3
  SecondAngle = 0
FEATURE [Part::Cylinder] Cylinder105
  Angle = 360
  AttacherType = Attacher::AttachEngine3D
  FirstAngle = 0
  Height = 10
  Placement = pos=(-398.15,100.55,100) rot=(0,0,1;0rad)
  Radius = 1.25
  SecondAngle = 0
FEATURE [Part::Cylinder] Cylinder106
  Angle = 360
  AttacherType = Attacher::AttachEngine3D
  FirstAngle = 0
  Height = 10
  Placement = pos=(-418.46,100.54,100) rot=(0,0,1;0rad)
  Radius = 1.25
  SecondAngle = 0
FEATURE [Part::Cylinder] Cylinder107
  Angle = 360
  AttacherType = Attacher::AttachEngine3D
  FirstAngle = 0
  Height = 10
  Placement = pos=(-418.46,120.86,100) rot=(0,0,1;0rad)
  Radius = 1.25
  SecondAngle = 0
FEATURE [Part::Cylinder] Cylinder108
  Angle = 360
  AttacherType = Attacher::AttachEngine3D
  FirstAngle = 0
  Height = 10
  Placement = pos=(-398.14,120.86,100) rot=(0,0,1;0rad)
  Radius = 1.25
  SecondAngle = 0
FEATURE [Part::MultiFuse] Fusion125  label="m2_cylinder"
  Placement = pos=(0,0,-43) rot=(0,0,1;0rad)
  Shapes = -> [Cylinder105,Cylinder106,Cylinder107,Cylinder108]
FEATURE [Part::Feature] Part__Feature192  label="Board"
  shape: bbox 25.4 x 25.4 x 1.57 mm, 211 faces (baked)
FEATURE [Part::Feature] Part__Feature193  label="QFN24_4MM"
  Placement = pos=(12.1412,14.4526,1.57) rot=(0,0,1;3.92699rad)
  shape: bbox 5.657 x 5.657 x 0.9 mm, 172 faces (baked)
FEATURE [Part::Feature] Part__Feature194  label="Part 5"
  shape: bbox 0.48 x 0.6603 x 0.6 mm, 14 faces (baked)
FEATURE [Part::Feature] Part__Feature195  label="Part 6"
  shape: bbox 0.48 x 0.6603 x 0.6 mm, 14 faces (baked)
FEATURE [Part::Feature] Part__Feature196  label="Part 4"
  shape: bbox 0.48 x 0.6603 x 0.6 mm, 14 faces (baked)
FEATURE [Part::Feature] Part__Feature197  label="Part 3"
  shape: bbox 0.48 x 0.6603 x 0.6 mm, 14 faces (baked)
FEATURE [Part::Feature] Part__Feature198  label="Part 2"
  shape: bbox 0.48 x 0.6603 x 0.6 mm, 14 faces (baked)
FEATURE [Part::Feature] Part__Feature199  label="Part 1"
  shape: bbox 3 x 1.4 x 1 mm, 10 faces (baked)
FEATURE [Part::Feature] Part__Feature200  label="Pin1"
  shape: bbox 0.6224 x 1.252 x 1.252 mm, 37 faces (baked)
FEATURE [Part::Feature] Part__Feature201  label="Pin2"
  shape: bbox 0.6224 x 1.252 x 1.252 mm, 37 faces (baked)
FEATURE [Part::Feature] Part__Feature202  label="CeramicBody"
  shape: bbox 1.8 x 1.23 x 1.23 mm, 10 faces (baked)
FEATURE [Part::Feature] Part__Feature203  label="0603-NO (1)"
  Placement = pos=(23.241,6.223,1.57) rot=(0,0,1;0rad)
  shape: bbox 1.7 x 0.9 x 0.55 mm, 52 faces, 3 solids (baked)
FEATURE [Part::Feature] Part__Feature204  label="0603-NO (2)"
  Placement = pos=(13.3858,8.4328,1.57) rot=(0,0,1;0rad)
  shape: bbox 1.7 x 0.9 x 0.55 mm, 52 faces, 3 solids (baked)
FEATURE [Part::Feature] Part__Feature205  label="0603-NO (3)"
  Placement = pos=(1.905,18.923,1.57) rot=(0,0,1;3.14159rad)
  shape: bbox 1.7 x 0.9 x 0.55 mm, 52 faces, 3 solids (baked)
FEATURE [Part::Feature] Part__Feature206  label="Pin1 (1)"
  shape: bbox 0.6224 x 1.252 x 1.252 mm, 37 faces (baked)
FEATURE [Part::Feature] Part__Feature207  label="Pin2 (1)"
  shape: bbox 0.6224 x 1.252 x 1.252 mm, 37 faces (baked)
FEATURE [Part::Feature] Part__Feature208  label="CeramicBody (1)"
  shape: bbox 1.8 x 1.23 x 1.23 mm, 10 faces (baked)
FEATURE [Part::Feature] Part__Feature209  label="Pin1 (2)"
  shape: bbox 0.6224 x 1.252 x 1.252 mm, 37 faces (baked)
FEATURE [Part::Feature] Part__Feature210  label="Pin2 (2)"
  shape: bbox 0.6224 x 1.252 x 1.252 mm, 37 faces (baked)
FEATURE [Part::Feature] Part__Feature211  label="CeramicBody (2)"
  shape: bbox 1.8 x 1.23 x 1.23 mm, 10 faces (baked)
FEATURE [Part::Feature] Part__Feature212  label="CHIPLED_0603_NOOUTLINE"
  Placement = pos=(23.368,8.509,1.57) rot=(0,0,1;1.5708rad)
  shape: bbox 1.616 x 0.8 x 0.4 mm, 133 faces (baked)
FEATURE [Part::Feature] Part__Feature213  label="CHIPLED_0603_NOOUTLINE (1)"
  Placement = pos=(1.905,16.764,1.57) rot=(0,0,-1;1.5708rad)
  shape: bbox 1.616 x 0.8 x 0.4 mm, 133 faces (baked)
FEATURE [Part::Feature] Part__Feature214  label="JST_SH4"
  Placement = pos=(22.86,12.7,1.57) rot=(0,0,1;1.5708rad)
  shape: bbox 4.95 x 6 x 2.96 mm, 229 faces, 7 solids (baked)
FEATURE [Part::Feature] Part__Feature215  label="JST_SH4 (1)"
  Placement = pos=(2.54,12.7,1.57) rot=(0,0,-1;1.5708rad)
  shape: bbox 4.95 x 6 x 2.96 mm, 229 faces, 7 solids (baked)
FEATURE [Part::Feature] Part__Feature216  label="NEO3535_REVERSE"
  Placement = pos=(12.7,23.114,0) rot=(0,1,0;3.14159rad)
  shape: bbox 5.88 x 2.8 x 1.78 mm, 41 faces, 5 solids (baked)
FEATURE [Part::Feature] Part__Feature217  label="RESPACK_4X0603"
  Placement = pos=(22.86,18.415,1.57) rot=(0,0,1;3.14159rad)
  shape: bbox 3.2 x 1.6 x 0.61 mm, 172 faces (baked)
FEATURE [Part::Feature] Part__Feature218  label="SOT363"
  Placement = pos=(17.399,12.192,1.57) rot=(0,0,-1;1.5708rad)
  shape: bbox 2.208 x 2.208 x 1.121 mm, 178 faces, 4 solids (baked)
FEATURE [Part::Feature] Part__Feature219  label="Body004"
  shape: bbox 15.5 x 16.75 x 29 mm, 21 faces (baked)
FEATURE [Part::Feature] Part__Feature220  label="Body005"
  Placement = pos=(0,0,2) rot=(0,0,1;0rad)
  shape: bbox 17.44 x 17.44 x 14.25 mm, 14 faces (baked)
FEATURE [Part::Feature] Part__Feature221  label="Body006"
  Placement = pos=(0,0,-5.5) rot=(0,0,1;0rad)
  shape: bbox 19 x 19 x 4.75 mm, 25 faces (baked)
FEATURE [Part::Feature] Part__Feature222  label="Body007"
  shape: bbox 16.75 x 16.75 x 0.9 mm, 4 faces (baked)
FEATURE [App::Part] PG7_Gland002
  Group = -> [Part__Feature219,Part__Feature220,Part__Feature221,Part__Feature222]
  Origin = -> Origin045
  Placement = pos=(-433,57,24) rot=(-0.258819,0.965926,0;3.14159rad)
FEATURE [Sketcher::SketchObject] Sketch005
  ArcFitTolerance = 0
  FullyConstrained = true
  MakeInternals = false
  sketch-geometry (39):
    g0: LineSegment StartX=3 StartY=43.5 StartZ=0 EndX=3 EndY=34.5 EndZ=0
    g1: LineSegment StartX=3 StartY=34.5 StartZ=0 EndX=70.5 EndY=34.5 EndZ=0
    g2: LineSegment StartX=3 StartY=43.5 StartZ=0 EndX=10.5 EndY=43.5 EndZ=0
    g3: LineSegment StartX=3 StartY=71 StartZ=0 EndX=10.5 EndY=71 EndZ=0
    g4: LineSegment StartX=3 StartY=71 StartZ=0 EndX=3 EndY=80 EndZ=0
    g5: LineSegment StartX=70.5 StartY=80 StartZ=0 EndX=70.5 EndY=71 EndZ=0
    g6: LineSegment StartX=70.5 StartY=71 StartZ=0 EndX=62.5 EndY=71 EndZ=0
    g7: LineSegment StartX=62.5 StartY=71 StartZ=0 EndX=62.5 EndY=43 EndZ=0
    g8: LineSegment StartX=62.5 StartY=43 StartZ=0 EndX=70.5 EndY=43 EndZ=0
    g9: LineSegment StartX=70.5 StartY=43 StartZ=0 EndX=70.5 EndY=34.5 EndZ=0
    g10: GeomPoint [constr] X=70.5 Y=34.5 Z=0
    g11: GeomPoint [constr] X=70.5 Y=34.5 Z=0
    g12: GeomPoint [constr] X=70.5 Y=34.5 Z=0
    g13: GeomPoint [constr] X=70.5 Y=34.5 Z=0
    g14: GeomPoint [constr] X=70.5 Y=34.5 Z=0
    g15: LineSegment StartX=10.5 StartY=43.5 StartZ=0 EndX=10.5 EndY=71 EndZ=0
    g16: Circle CenterX=7.5 CenterY=75.5 CenterZ=0 NormalX=0 NormalY=0 NormalZ=1 AngleXU=0 Radius=1.6
    g17: Circle CenterX=7.5 CenterY=39 CenterZ=0 NormalX=0 NormalY=0 NormalZ=1 AngleXU=0 Radius=1.6
    g18: Circle CenterX=66.5 CenterY=39 CenterZ=0 NormalX=0 NormalY=0 NormalZ=1 AngleXU=0 Radius=1.6
    g19: Circle CenterX=66.5 CenterY=75.5 CenterZ=0 NormalX=0 NormalY=0 NormalZ=1 AngleXU=0 Radius=1.6
    g20: Circle CenterX=14.2 CenterY=70.46 CenterZ=0 NormalX=0 NormalY=0 NormalZ=1 AngleXU=0 Radius=1.6
    g21: Circle CenterX=38.54 CenterY=77.84 CenterZ=0 NormalX=0 NormalY=0 NormalZ=1 AngleXU=0 Radius=1.6
    g22: Circle CenterX=58.86 CenterY=77.84 CenterZ=0 NormalX=0 NormalY=0 NormalZ=1 AngleXU=0 Radius=1.6
    g23: Circle CenterX=38.54 CenterY=57.52 CenterZ=0 NormalX=0 NormalY=0 NormalZ=1 AngleXU=0 Radius=1.6
    g24: Circle CenterX=58.86 CenterY=57.52 CenterZ=0 NormalX=0 NormalY=0 NormalZ=1 AngleXU=0 Radius=1.6
    g25: Circle CenterX=38.54 CenterY=52.33 CenterZ=0 NormalX=0 NormalY=0 NormalZ=1 AngleXU=0 Radius=1.6
    g26: Circle CenterX=58.86 CenterY=52.33 CenterZ=0 NormalX=0 NormalY=0 NormalZ=1 AngleXU=0 Radius=1.6
    g27: Circle CenterX=38.54 CenterY=39.63 CenterZ=0 NormalX=0 NormalY=0 NormalZ=1 AngleXU=0 Radius=1.6
    g28: Circle CenterX=58.86 CenterY=39.63 CenterZ=0 NormalX=0 NormalY=0 NormalZ=1 AngleXU=0 Radius=1.6
    g29: Circle CenterX=30.43 CenterY=38.46 CenterZ=0 NormalX=0 NormalY=0 NormalZ=1 AngleXU=0 Radius=1.6
    g30: ArcOfCircle CenterX=48.54 CenterY=70.34 CenterZ=0 NormalX=0 NormalY=0 NormalZ=1 AngleXU=0 Radius=5 StartAngle=-9e-16 EndAngle=3.14159
    g31: ArcOfCircle CenterX=48.54 CenterY=42.63 CenterZ=0 NormalX=0 NormalY=0 NormalZ=1 AngleXU=0 Radius=5 StartAngle=3.14159 EndAngle=6.28319
    g32: LineSegment StartX=43.54 StartY=70.34 StartZ=0 EndX=43.54 EndY=42.63 EndZ=0
    g33: LineSegment StartX=53.54 StartY=42.63 StartZ=0 EndX=53.54 EndY=70.34 EndZ=0
    g34: ArcOfCircle CenterX=22.2 CenterY=70.34 CenterZ=0 NormalX=0 NormalY=0 NormalZ=1 AngleXU=0 Radius=5 StartAngle=0 EndAngle=3.14159
    g35: ArcOfCircle CenterX=22.2 CenterY=42.63 CenterZ=0 NormalX=0 NormalY=0 NormalZ=1 AngleXU=0 Radius=5 StartAngle=3.14159 EndAngle=6.28319
    g36: LineSegment StartX=17.2 StartY=70.34 StartZ=0 EndX=17.2 EndY=42.63 EndZ=0
    g37: LineSegment StartX=27.2 StartY=42.63 StartZ=0 EndX=27.2 EndY=70.34 EndZ=0
    g38: LineSegment StartX=3 StartY=80 StartZ=0 EndX=70.5 EndY=80 EndZ=0
  constraints (103):
    c: Vertical(g0)
    c: Coincident(g1,g0)
    c: Horizontal(g1)
    c: Coincident(g2,g0)
    c: Coincident(g4,g3)
    c: Vertical(g4)
    c: Coincident(g6,g5)
    c: Horizontal(g6)
    c: Coincident(g7,g6)
    c: Vertical(g7)
    c: Horizontal(g8)
    c: Horizontal(g2)
    c: Coincident(g10,g9)
    c: Coincident(g11,g1)
    c: Coincident(g12,g9)
    c: Coincident(g13,g1)
    c: Coincident(g14,g9)
    c: Coincident(g9,g1)
    c: Vertical(g9)
    c: Coincident(g15,g2)
    c: Coincident(g15,g3)
    c: Vertical(g15)
    c: Horizontal(g3)
    c: Vertical(g5)
    c: Coincident(g8,g9)
    c: Coincident(g7,g8)
    c: DistanceX(g8,g8) = 8
    c: Radius(g16) = 1.6
    c: DistanceY(g17) = 39
    c: Radius(g17) = 1.6
    c: DistanceX(g18) = 66.5
    c: DistanceY(g17,g18) = 0
    c: Radius(g18) = 1.6
    c: DistanceX(g19,g18) = 0
    c: Radius(g19) = 1.6
    c: DistanceY(g16) = 75.5
    c: DistanceY(g16,g19) = 0
    c: DistanceY(g3,g5) = 0
    c: Radius(g21) = 1.6
    c: DistanceY(g21,g22) = 0
    c: Radius(g22) = 1.6
    c: DistanceX(g21,g22) = 20.32
    c: DistanceX(g23,g21) = 0
    c: Radius(g23) = 1.6
    c: DistanceY(g23,g21) = 20.32
    c: DistanceY(g24,g23) = 0
    c: DistanceX(g24,g22) = 0
    c: Radius(g24) = 1.6
    c: DistanceX(g25,g23) = 0
    c: Radius(g25) = 1.6
    c: DistanceY(g25,g26) = 0
    c: DistanceX(g24,g26) = 0
    c: Radius(g26) = 1.6
    c: DistanceX(g25,g27) = 0
    c: DistanceX(g28,g26) = 0
    c: DistanceY(g27,g25) = 12.7
    c: DistanceY(g28,g27) = 0
    c: Radius(g28) = 1.6
    c: Radius(g27) = 1.6
    c: Radius(g29) = 1.6
    c: DistanceY(g29,g20) = 32
    c: Radius(g20) = 1.6
    c: Tangent(g30,g32) = -1.5708
    c: Tangent(g32,g31) = -1.5708
    c: Tangent(g31,g33) = -1.5708
    c: Tangent(g33,g30) = -1.5708
    c: Equal(g30,g31)
    c: Vertical(g32)
    c: DistanceY(g27,g31) = 3
    c: Radius(g30) = 5
    c: Tangent(g34,g36) = -1.5708
    c: Tangent(g36,g35) = -1.5708
    c: Tangent(g35,g37) = -1.5708
    c: Tangent(g37,g34) = -1.5708
    c: Equal(g34,g35)
    c: Vertical(g36)
    c: Radius(g34) = 5
    c: DistanceY(g34,g30) = 0
    c: DistanceY(g31,g35) = 0
    c: DistanceX(g16,g17) = 0
    c: DistanceX(g0,g3) = 0
    c: Coincident(g38,g4)
    c: Coincident(g38,g5)
    c: Horizontal(g38)
    c: DistanceX(g29) = 30.43
    c: DistanceX(g20) = 14.2
    c: DistanceY(g20) = 70.46
    c: DistanceX(g27) = 38.54
    c: DistanceY(g27) = 39.63
    c: DistanceY(g23) = 57.52
    c: DistanceY(g3,g16) = 4.5
    c: DistanceY(g16,g4) = 4.5
    c: DistanceY(g0,g17) = 4.5
    c: DistanceX(g0,g17) = 4.5
    c: DistanceX(g17) = 7.5
    c: DistanceY(g17,g0) = 4.5
    c: DistanceX(g16,g3) = 3
    c: DistanceX(g19,g5) = 4
    c: DistanceX(g6,g19) = 4
    c: DistanceY(g18,g8) = 4
    c: DistanceX(g25,g31) = 10
    c: DistanceY(g30,g21) = 7.5
    c: DistanceX(g20,g34) = 8
FEATURE [Part::Extrusion] Extrude005  label="sensorHold"
  Base = -> Sketch005
  Dir = (0,0,1)
  DirMode = 2
  FaceMakerClass = Part::FaceMakerBullseye
  FaceMakerMode = 3
  LengthFwd = 4
  LengthRev = 0
  Placement = pos=(0,0,16) rot=(0,0,1;0rad)
  Solid = true
  Symmetric = false
FEATURE [Part::Fillet] Fillet006  label="sensorHold001"
  Base = -> Extrude005
  EdgeLinks = -> Extrude005 [Edge1,Edge2,Edge5,Edge8,Edge11,Edge14,Edge17,Edge20,Edge23,Edge26,Edge29,Edge32]
  Edges = 12 edges r=3: [Edge1,Edge2,Edge5,Edge8,Edge11,Edge14,Edge17,Edge20,Edge23,Edge26,Edge29,Edge32]
FEATURE [Part::Torus] Torus003
  Angle1 = -180
  Angle2 = 180
  Angle3 = 180
  AttacherType = Attacher::AttachEngine3D
  Placement = pos=(-63.5,61,76.5) rot=(0,0.707107,0.707107;3.14159rad)
  Radius1 = 15.8
  Radius2 = 3
FEATURE [Part::Torus] Torus004
  Angle1 = -180
  Angle2 = 180
  Angle3 = 180
  AttacherType = Attacher::AttachEngine3D
  Placement = pos=(-63.5,61,76.5) rot=(0,0.707107,0.707107;3.14159rad)
  Radius1 = 15.8
  Radius2 = 3
FEATURE [Part::FeaturePython] Tube006  # WARN: FeaturePython — macro-defined, semantics opaque (R4)
  AttacherType = Attacher::AttachEngine3D
  Height = 10
  InnerRadius = 2
  OuterRadius = 4
  Placement = pos=(-76.3,61,59) rot=(0,-1,0;1.5708rad)
FEATURE [Part::FeaturePython] Tube007  # WARN: FeaturePython — macro-defined, semantics opaque (R4)
  AttacherType = Attacher::AttachEngine3D
  Height = 10
  InnerRadius = 2
  OuterRadius = 4
  Placement = pos=(-40.7,61,59) rot=(0,-1,0;1.5708rad)
FEATURE [App::Part] Part002  label="pipe_hold"
  Group = -> [Torus003,Cylinder101,Cylinder102,Tube006,Tube007]
  Origin = -> Origin046
  Placement = pos=(-481,40,-66) rot=(0,0,1;4.71239rad)
FEATURE [Part::MultiFuse] Fusion122
  Placement = pos=(-15,0,0) rot=(0,0,1;0rad)
  Shapes = -> [Box207,Box208,Box209,Box210,Part002]
FEATURE [Part::FeaturePython] Tube008  # WARN: FeaturePython — macro-defined, semantics opaque (R4)
  AttacherType = Attacher::AttachEngine3D
  Height = 10
  InnerRadius = 2
  OuterRadius = 4
  Placement = pos=(-76.3,61,59) rot=(0,-1,0;1.5708rad)
FEATURE [Part::FeaturePython] Tube009  # WARN: FeaturePython — macro-defined, semantics opaque (R4)
  AttacherType = Attacher::AttachEngine3D
  Height = 10
  InnerRadius = 2
  OuterRadius = 4
  Placement = pos=(-40.7,61,59) rot=(0,-1,0;1.5708rad)
FEATURE [App::Part] Part003  label="pipe_hold001"
  Group = -> [Torus004,Cylinder103,Cylinder104,Tube008,Tube009]
  Origin = -> Origin047
  Placement = pos=(-481,40,-66) rot=(0,0,1;4.71239rad)
FEATURE [Part::MultiFuse] Fusion123
  Placement = pos=(15,0,0) rot=(0,0,1;0rad)
  Shapes = -> [Box211,Box212,Box213,Box214,Part003]
FEATURE [Part::MultiFuse] Fusion124  label="Holder_Bottom"
  Shapes = -> [Box204,Box205,Box206,Fusion122,Fusion123,Cut011]
FEATURE [Part::Cut] Cut012  label="Holder_btm"
  Base = -> Fusion124
  Tool = -> Fusion125
FEATURE [Part::Fillet] Fillet007
  Base = -> Cut012
  EdgeLinks = -> Cut012 [Edge65,Edge67]
  Edges = 2 edges r=1: [Edge65,Edge67]
FEATURE [Part::Fillet] Fillet008
  Base = -> Fillet007
  EdgeLinks = -> Fillet007 [Edge151]
  Edges = 1 edges r=1: [Edge151]
FEATURE [App::Part] _603_NO  label="0603-NO"
  Group = -> [Part__Feature200,Part__Feature201,Part__Feature202]
  Origin = -> Origin039
  Placement = pos=(16.51,8.382,1.57) rot=(0,0,1;0rad)
FEATURE [App::Part] _6700497  label="36700497"
  Group = -> [Part__Feature194,Part__Feature195,Part__Feature196,Part__Feature197,Part__Feature198,Part__Feature199]
  Origin = -> Origin038
  Placement = pos=(0,0,0) rot=(0,0,1;3.14159rad)
FEATURE [App::Part] SOT23_5  label="SOT23-5"
  Group = -> [_6700497]
  Origin = -> Origin009
  Placement = pos=(2.54,6.985,1.57) rot=(0,0,1;3.14159rad)
FEATURE [App::Part] _805_NO  label="0805-NO"
  Group = -> [Part__Feature206,Part__Feature207,Part__Feature208]
  Origin = -> Origin040
  Placement = pos=(7.874,13.589,1.57) rot=(0,0,1;1.5708rad)
FEATURE [App::Part] _805_NO__1_  label="0805-NO (1)"
  Group = -> [Part__Feature209,Part__Feature210,Part__Feature211]
  Origin = -> Origin041
  Placement = pos=(12.827,6.223,1.57) rot=(0,0,1;3.14159rad)
FEATURE [App::Part] Packages
  Group = -> [Part__Feature193,SOT23_5,_603_NO,Part__Feature203,Part__Feature204,Part__Feature205,_805_NO,_805_NO__1_,Part__Feature212,Part__Feature213,Part__Feature214,Part__Feature215,Part__Feature216,Part__Feature217,Part__Feature218]
  Origin = -> Origin042
FEATURE [App::Part] Adafruit_I2C_QT_Rotary_Encoder_v2  label="gps"
  Group = -> [Part__Feature192,Packages,Sketch005,Extrude005,Fillet006]
  Origin = -> Origin043
  Placement = pos=(-421,98,65) rot=(0,0,1;0rad)
FEATURE [App::Part] Part001  label="GPS_holder"
  Group = -> [Adafruit_I2C_QT_Rotary_Encoder_v2,PG7_Gland002,Box207,Box202,Box205,Box206,Box203,Box204,Part002,Part003,Cut011,Fusion123,Fusion124,Fusion122,Fusion125,Cylinder107,Cylinder105,Cylinder108,Cylinder106,Box208,Box209,Box211,Box210,Box213,Box214,Box212,Cut012,Fillet007,Fillet008]
  Origin = -> Origin044
  Placement = pos=(-167,0,66) rot=(0,0,1;4.71239rad)
